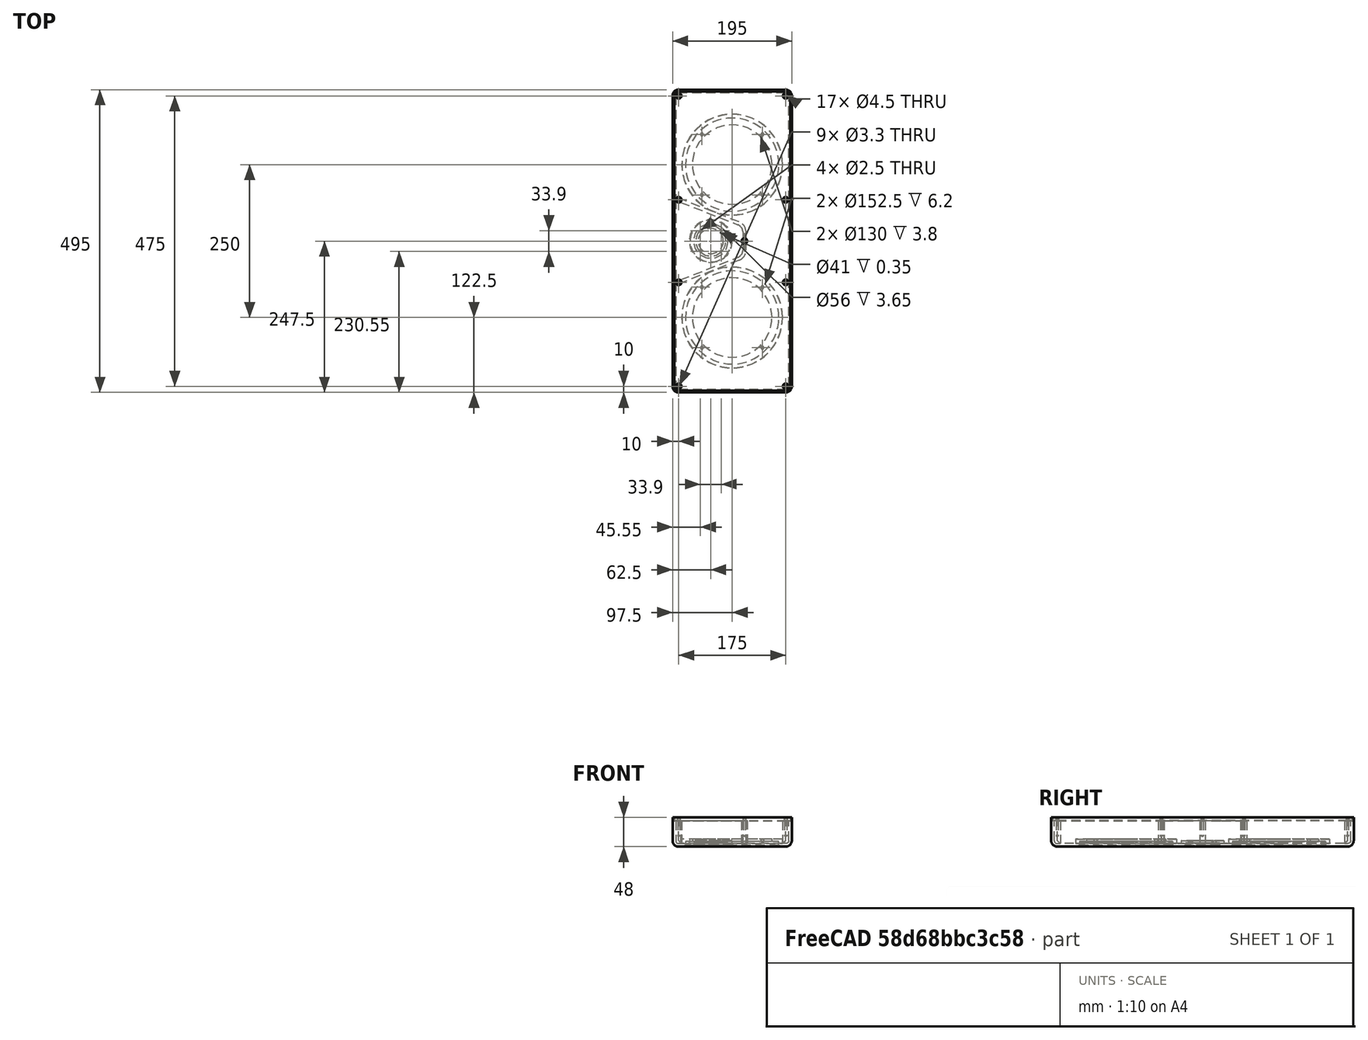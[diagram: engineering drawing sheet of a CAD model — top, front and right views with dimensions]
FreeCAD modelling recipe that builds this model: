
FCSTD DOCUMENT  (FreeCAD 1.1R20260223 (Git shallow))
Label: wallspeakers prototype v6.1
License: All rights reserved
LicenseURL: http://en.wikipedia.org/wiki/All_rights_reserved
objects: TechDraw::DrawViewDimension×43, Sketcher::SketchObject×17, TechDraw::DrawViewAnnotation×7, PartDesign::Pad×6, PartDesign::Pocket×5, TechDraw::DrawProjGroupItem×5, TechDraw::DrawSVGTemplate×4, PartDesign::Hole×4, TechDraw::DrawPage×4, PartDesign::Chamfer×3, App::Point×2, PartDesign::Body×2, TechDraw::DrawViewImage×2, Part::Feature×2, App::VarSet×1, PartDesign::Fillet×1, PartDesign::Thickness×1, App::DocumentObjectGroup×1
note: 167 computed .brp shape members not serialized (recipe doc carries the construction recipe); baked Part::Feature solids carry a one-line shape summary decoded from their .brp

FEATURE [Sketcher::SketchObject] Sketch002  label="base geometry"
  ArcFitTolerance = 1e-06
  AttachmentSupport = -> [XY_Plane]
  ExternalTypes = [0]
  FullyConstrained = true
  MakeInternals = false
  MapMode = 5
  expr: Constraints[3] = <<v>>.bmr_offset
  expr: Constraints[4] = <<v>>.woofer_offset
  expr: Constraints[5] = <<v>>.woofer_offset
  expr: Constraints[6] = <<v>>.ext_height / 2
  expr: Constraints[7] = <<v>>.ext_width / 2
  sketch-geometry (7):
    g0: GeomPoint [constr] X=-97.5 Y=247.5 Z=0
    g1: GeomPoint [constr] X=97.5 Y=247.5 Z=0
    g2: GeomPoint [constr] X=97.5 Y=-247.5 Z=0
    g3: GeomPoint [constr] X=-97.5 Y=-247.5 Z=0
    g4: GeomPoint [constr] X=-35 Y=0 Z=0
    g5: GeomPoint [constr] X=0 Y=125 Z=0
    g6: GeomPoint [constr] X=0 Y=-125 Z=0
  constraints (11):
    c: PointOnObject(g4,g-1)
    c: PointOnObject(g5,g-2)
    c: PointOnObject(g6,g-2)
    c: DistanceX(g4,g-1) = 35
    c: DistanceY(g-1,g5) = 125
    c: DistanceY(g6,g-1) = 125
    c: DistanceY(g-1,g1) = 247.5
    c: DistanceX(g-1,g1) = 97.5
    c: Symmetric(g0,g1,g-2)
    c: Symmetric(g1,g2,g-1)
    c: Symmetric(g3,g2,g-2)
FEATURE [Sketcher::SketchObject] Sketch  label="back panel screw hole geometry"
  ArcFitTolerance = 1e-06
  AttachmentSupport = -> [Sketch002]
  ExternalTypes = [0]
  FullyConstrained = true
  MakeInternals = false
  MapMode = 2
  expr: Constraints[11] = <<v>>.bmr_enc_offset
  expr: Constraints[1] = <<v>>.ext_height / 2 - <<v>>.screw_inset
  expr: Constraints[2] = <<v>>.ext_width / 2 - <<v>>.screw_inset
  expr: Constraints[8] = <<v>>.ext_width / 2 - <<v>>.screw_inset
  expr: Constraints[9] = <<v>>.bmr_enc_base
  sketch-geometry (9):
    g0: GeomPoint [constr] X=-87.5 Y=237.5 Z=0
    g1: GeomPoint [constr] X=87.5 Y=237.5 Z=0
    g2: GeomPoint [constr] X=87.5 Y=-237.5 Z=0
    g3: GeomPoint [constr] X=-87.5 Y=-237.5 Z=0
    g4: GeomPoint [constr] X=-87.5 Y=-67.5 Z=0
    g5: GeomPoint [constr] X=-87.5 Y=67.5 Z=0
    g6: GeomPoint [constr] X=87.5 Y=67.5 Z=0
    g7: GeomPoint [constr] X=87.5 Y=-67.5 Z=0
    g8: GeomPoint [constr] X=20 Y=0 Z=0
  constraints (12):
    c: PointOnObject(g8,g-1)
    c: DistanceY(g-1,g0) = 237.5
    c: DistanceX(g0,g-1) = 87.5
    c: Symmetric(g0,g1,g-2)
    c: Symmetric(g5,g6,g-2)
    c: Symmetric(g4,g7,g-2)
    c: Symmetric(g3,g2,g-2)
    c: Symmetric(g2,g1,g-1)
    c: DistanceX(g5,g-1) = 87.5
    c: DistanceY(g4,g5) = 135
    c: Symmetric(g5,g4,g-1)
    c: DistanceX(g-1,g8) = 20
FEATURE [App::VarSet] VarSet001  label="v"
  backplate_height = 489.8
  backplate_rebate = 5.9
  backplate_thickness = 5
  backplate_width = 189.8
  bmr_enc_base = 135
  bmr_enc_offset = 20
  bmr_enc_top = 50
  bmr_hole_dia = 41
  bmr_offset = 35
  bmr_plate_thickness = 2.75
  bmr_rebate_depth = 5.65
  bmr_rebate_dia = 56
  bmr_support_dia = 70
  bmr_support_thickness = 5
  ext_depth = 48
  ext_height = 495
  ext_roundover = 10
  ext_wall = 5
  ext_width = 195
  gasket_thickness = 0.9
  int_depth = 37.1
  rim_width = 2.5
  screw_inset = 10
  screw_post_diameter = 10
  surround_chamfer = 2
  woofer_cutout_dia = 130
  woofer_offset = 125
  woofer_plate_thickness = 5.3
  woofer_rebate_depth = 8.2
  woofer_rebate_dia = 152.5
  woofer_support_dia = 165
  woofer_support_thickness = 7
  expr: backplate_height = ext_height - rim_width * 2 - 0.2 mm
  expr: backplate_rebate = ext_wall + gasket_thickness
  expr: backplate_width = ext_width - rim_width * 2 - 0.2 mm
  expr: bmr_rebate_depth = bmr_plate_thickness + gasket_thickness + surround_chamfer
  expr: int_depth = ext_depth - ext_wall - backplate_rebate
  expr: woofer_rebate_depth = woofer_plate_thickness + gasket_thickness + surround_chamfer
FEATURE [App::Point] Origin001
  Role = Origin
FEATURE [Sketcher::SketchObject] Sketch003  label="main body"
  ArcFitTolerance = 1e-06
  AttachmentSupport = -> [Sketch002]
  ExternalTypes = [0]
  FullyConstrained = true
  MakeInternals = false
  MapMode = 2
  expr: Constraints[32] = <<v>>.ext_roundover
  expr: Constraints[3] = Sketch002.Constraints[3]
  expr: Constraints[4] = Sketch002.Constraints[4]
  expr: Constraints[5] = Sketch002.Constraints[5]
  expr: Constraints[6] = Sketch002.Constraints[6]
  expr: Constraints[7] = Sketch002.Constraints[7]
  sketch-geometry (17):
    g0: GeomPoint [constr] X=-97.5 Y=247.5 Z=0
    g1: GeomPoint [constr] X=97.5 Y=247.5 Z=0
    g2: GeomPoint [constr] X=97.5 Y=-247.5 Z=0
    g3: GeomPoint [constr] X=-97.5 Y=-247.5 Z=0
    g4: GeomPoint [constr] X=-35 Y=0 Z=0
    g5: GeomPoint [constr] X=0 Y=125 Z=0
    g6: GeomPoint [constr] X=0 Y=-125 Z=0
    g7: LineSegment StartX=-97.5 StartY=237.5 StartZ=0 EndX=-97.5 EndY=-237.5 EndZ=0
    g8: LineSegment StartX=-87.5 StartY=-247.5 StartZ=0 EndX=87.5 EndY=-247.5 EndZ=0
    g9: LineSegment StartX=97.5 StartY=-237.5 StartZ=0 EndX=97.5 EndY=237.5 EndZ=0
    g10: LineSegment StartX=87.5 StartY=247.5 StartZ=0 EndX=-87.5 EndY=247.5 EndZ=0
    g11: ArcOfCircle CenterX=-87.5 CenterY=237.5 CenterZ=0 NormalX=0 NormalY=0 NormalZ=1 AngleXU=0 Radius=10 StartAngle=1.5708 EndAngle=3.14159
    g12: ArcOfCircle CenterX=-87.5 CenterY=-237.5 CenterZ=0 NormalX=0 NormalY=0 NormalZ=1 AngleXU=0 Radius=10 StartAngle=3.14159 EndAngle=4.71239
    g13: ArcOfCircle CenterX=87.5 CenterY=-237.5 CenterZ=0 NormalX=0 NormalY=0 NormalZ=1 AngleXU=0 Radius=10 StartAngle=4.71239 EndAngle=6.28319
    g14: ArcOfCircle CenterX=87.5 CenterY=237.5 CenterZ=0 NormalX=0 NormalY=0 NormalZ=1 AngleXU=0 Radius=10 StartAngle=-3.2e-14 EndAngle=1.5708
    g15: GeomPoint [constr] X=-97.5 Y=247.5 Z=0
    g16: GeomPoint [constr] X=97.5 Y=-247.5 Z=0
  constraints (33):
    c: PointOnObject(g4,g-1)
    c: PointOnObject(g5,g-2)
    c: PointOnObject(g6,g-2)
    c: DistanceX(g4,g-1) = 35
    c: DistanceY(g-1,g5) = 125
    c: DistanceY(g6,g-1) = 125
    c: DistanceY(g-1,g1) = 247.5
    c: DistanceX(g-1,g1) = 97.5
    c: Symmetric(g0,g1,g-2)
    c: Symmetric(g1,g2,g-1)
    c: Symmetric(g3,g2,g-2)
    c: Tangent(g7,g11) = -1.5708
    c: Tangent(g7,g12) = -1.5708
    c: Tangent(g8,g12) = -1.5708
    c: Tangent(g8,g13) = -1.5708
    c: Tangent(g9,g13) = -1.5708
    c: Tangent(g9,g14) = -1.5708
    c: Tangent(g10,g14) = -1.5708
    c: Tangent(g10,g11) = -1.5708
    c: Vertical(g7)
    c: Vertical(g9)
    c: Horizontal(g8)
    c: Horizontal(g10)
    c: Equal(g11,g12)
    c: Equal(g12,g13)
    c: Equal(g13,g14)
    c: PointOnObject(g15,g7)
    c: PointOnObject(g15,g10)
    c: PointOnObject(g16,g8)
    c: PointOnObject(g16,g9)
    c: Coincident(g15,g0)
    c: Coincident(g16,g2)
    c: Radius(g11) = 10
FEATURE [PartDesign::Pad] Pad  label="main body pad"
  Direction = (0,0,1)
  Length = 48
  Length2 = 10
  Profile = -> Sketch003
  ReferenceAxis = -> Sketch003 [N_Axis]
  SideType = 0
  Suppressed = false
  Type = 0
  Type2 = 0
  expr: Length = <<v>>.ext_depth
FEATURE [PartDesign::Fillet] Fillet  label="main body front roundovers"
  Base = -> Pad [Face9]
  BaseFeature = -> Pad
  Radius = 10
  SupportTransform = false
  Suppressed = false
  UseAllEdges = false
  expr: Radius = <<v>>.ext_roundover
FEATURE [PartDesign::Thickness] Thickness  label="main body thicknessing"
  Base = -> Fillet [Face4]
  BaseFeature = -> Fillet
  Intersection = false
  Join = 0
  Mode = 0
  Reversed = true
  SupportTransform = false
  Suppressed = false
  Value = 5
  expr: Value = <<v>>.ext_wall
FEATURE [Sketcher::SketchObject] Sketch004  label="screw posts layout"
  ArcFitTolerance = 1e-06
  AttachmentOffset = pos=(0,0,5) rot=(0,0,1;0rad)
  AttachmentSupport = -> [Sketch]
  ExternalTypes = [0]
  FullyConstrained = true
  MakeInternals = false
  MapMode = 2
  Placement = pos=(0,0,5) rot=(0,0,1;0rad)
  expr: .AttachmentOffset.Base.z = <<v>>.ext_wall
  expr: Constraints[12] = <<v>>.bmr_enc_offset
  expr: Constraints[13] = <<v>>.screw_post_diameter
  expr: Constraints[1] = Sketch.Constraints[1]
  expr: Constraints[22] = <<v>>.screw_post_diameter
  expr: Constraints[2] = Sketch.Constraints[2]
  expr: Constraints[8] = Sketch.Constraints[8]
  expr: Constraints[9] = Sketch.Constraints[9]
  sketch-geometry (18):
    g0: GeomPoint [constr] X=-87.5 Y=237.5 Z=0
    g1: GeomPoint [constr] X=87.5 Y=237.5 Z=0
    g2: GeomPoint [constr] X=87.5 Y=-237.5 Z=0
    g3: GeomPoint [constr] X=-87.5 Y=-237.5 Z=0
    g4: GeomPoint [constr] X=-87.5 Y=-67.5 Z=0
    g5: GeomPoint [constr] X=-87.5 Y=67.5 Z=0
    g6: GeomPoint [constr] X=87.5 Y=67.5 Z=0
    g7: GeomPoint [constr] X=87.5 Y=-67.5 Z=0
    g8: GeomPoint [constr] X=20 Y=0 Z=0
    g9: Circle CenterX=20 CenterY=0 CenterZ=0 NormalX=0 NormalY=0 NormalZ=1 AngleXU=0 Radius=5
    g10: Circle CenterX=-87.5 CenterY=237.5 CenterZ=0 NormalX=0 NormalY=0 NormalZ=1 AngleXU=0 Radius=5
    g11: Circle CenterX=87.5 CenterY=237.5 CenterZ=0 NormalX=0 NormalY=0 NormalZ=1 AngleXU=0 Radius=5
    g12: Circle CenterX=87.5 CenterY=67.5 CenterZ=0 NormalX=0 NormalY=0 NormalZ=1 AngleXU=0 Radius=5
    g13: Circle CenterX=-87.5 CenterY=67.5 CenterZ=0 NormalX=0 NormalY=0 NormalZ=1 AngleXU=0 Radius=5
    g14: Circle CenterX=87.5 CenterY=-67.5 CenterZ=0 NormalX=0 NormalY=0 NormalZ=1 AngleXU=0 Radius=5
    g15: Circle CenterX=-87.5 CenterY=-67.5 CenterZ=0 NormalX=0 NormalY=0 NormalZ=1 AngleXU=0 Radius=5
    g16: Circle CenterX=-87.5 CenterY=-237.5 CenterZ=0 NormalX=0 NormalY=0 NormalZ=1 AngleXU=0 Radius=5
    g17: Circle CenterX=87.5 CenterY=-237.5 CenterZ=0 NormalX=0 NormalY=0 NormalZ=1 AngleXU=0 Radius=5
  constraints (30):
    c: PointOnObject(g8,g-1)
    c: DistanceY(g-1,g0) = 237.5
    c: DistanceX(g0,g-1) = 87.5
    c: Symmetric(g0,g1,g-2)
    c: Symmetric(g5,g6,g-2)
    c: Symmetric(g4,g7,g-2)
    c: Symmetric(g3,g2,g-2)
    c: Symmetric(g2,g1,g-1)
    c: DistanceX(g5,g-1) = 87.5
    c: DistanceY(g4,g5) = 135
    c: Symmetric(g5,g4,g-1)
    c: Coincident(g9,g8)
    c: DistanceX(g-1,g8) = 20
    c: Diameter(g9) = 10
    c: Coincident(g10,g0)
    c: Coincident(g11,g1)
    c: Coincident(g12,g6)
    c: Coincident(g13,g5)
    c: Coincident(g14,g7)
    c: Coincident(g15,g4)
    c: Coincident(g16,g3)
    c: Coincident(g17,g2)
    c: Diameter(g10) = 10
    c: Equal(g10,g11)
    c: Equal(g11,g12)
    c: Equal(g12,g13)
    c: Equal(g13,g15)
    c: Equal(g15,g14)
    c: Equal(g14,g17)
    c: Equal(g17,g16)
FEATURE [Sketcher::SketchObject] Sketch005  label="woofer rebates"
  ArcFitTolerance = 1e-06
  AttachmentSupport = -> [Origin]
  ExternalTypes = [0]
  FullyConstrained = true
  MakeInternals = false
  MapMode = 5
  expr: Constraints[12] = VarSet001.woofer_rebate_dia
  expr: Constraints[3] = Sketch002.Constraints[3]
  expr: Constraints[4] = Sketch002.Constraints[4]
  expr: Constraints[5] = Sketch002.Constraints[5]
  expr: Constraints[6] = Sketch002.Constraints[6]
  expr: Constraints[7] = Sketch002.Constraints[7]
  sketch-geometry (9):
    g0: GeomPoint [constr] X=-97.5 Y=247.5 Z=0
    g1: GeomPoint [constr] X=97.5 Y=247.5 Z=0
    g2: GeomPoint [constr] X=97.5 Y=-247.5 Z=0
    g3: GeomPoint [constr] X=-97.5 Y=-247.5 Z=0
    g4: GeomPoint [constr] X=-35 Y=0 Z=0
    g5: GeomPoint [constr] X=0 Y=125 Z=0
    g6: GeomPoint [constr] X=0 Y=-125 Z=0
    g7: Circle CenterX=0 CenterY=125 CenterZ=0 NormalX=0 NormalY=0 NormalZ=1 AngleXU=0 Radius=76.25
    g8: Circle CenterX=0 CenterY=-125 CenterZ=0 NormalX=0 NormalY=0 NormalZ=1 AngleXU=0 Radius=76.25
  constraints (15):
    c: PointOnObject(g4,g-1)
    c: PointOnObject(g5,g-2)
    c: PointOnObject(g6,g-2)
    c: DistanceX(g4,g-1) = 35
    c: DistanceY(g-1,g5) = 125
    c: DistanceY(g6,g-1) = 125
    c: DistanceY(g-1,g1) = 247.5
    c: DistanceX(g-1,g1) = 97.5
    c: Symmetric(g0,g1,g-2)
    c: Symmetric(g1,g2,g-1)
    c: Symmetric(g3,g2,g-2)
    c: Coincident(g8,g6)
    c: Diameter(g7) = 152.5
    c: Equal(g7,g8)
    c: Coincident(g5,g7)
FEATURE [Sketcher::SketchObject] Sketch006
  ArcFitTolerance = 1e-06
  AttachmentOffset = pos=(0,0,5) rot=(0,0,1;0rad)
  AttachmentSupport = -> [Origin]
  ExternalTypes = [0]
  FullyConstrained = true
  MakeInternals = false
  MapMode = 5
  Placement = pos=(0,0,5) rot=(0,0,1;0rad)
  expr: .AttachmentOffset.Base.z = <<v>>.ext_wall
  expr: Constraints[14] = Sketch002.Constraints[3]
  expr: Constraints[15] = Sketch002.Constraints[4]
  expr: Constraints[16] = Sketch002.Constraints[5]
  expr: Constraints[17] = Sketch002.Constraints[6]
  expr: Constraints[18] = Sketch002.Constraints[7]
  expr: Constraints[22] = VarSet001.woofer_support_dia
  expr: Constraints[3] = Sketch002.Constraints[3]
  expr: Constraints[4] = Sketch002.Constraints[4]
  expr: Constraints[5] = Sketch002.Constraints[5]
  expr: Constraints[6] = Sketch002.Constraints[6]
  expr: Constraints[7] = Sketch002.Constraints[7]
  sketch-geometry (16):
    g0: GeomPoint [constr] X=-97.5 Y=247.5 Z=0
    g1: GeomPoint [constr] X=97.5 Y=247.5 Z=0
    g2: GeomPoint [constr] X=97.5 Y=-247.5 Z=0
    g3: GeomPoint [constr] X=-97.5 Y=-247.5 Z=0
    g4: GeomPoint [constr] X=-35 Y=0 Z=0
    g5: GeomPoint [constr] X=0 Y=125 Z=0
    g6: GeomPoint [constr] X=0 Y=-125 Z=0
    g7: GeomPoint [constr] X=-97.5 Y=247.5 Z=0
    g8: GeomPoint [constr] X=97.5 Y=247.5 Z=0
    g9: GeomPoint [constr] X=97.5 Y=-247.5 Z=0
    g10: GeomPoint [constr] X=-97.5 Y=-247.5 Z=0
    g11: GeomPoint [constr] X=-35 Y=0 Z=0
    g12: GeomPoint [constr] X=0 Y=125 Z=0
    g13: GeomPoint [constr] X=0 Y=-125 Z=0
    g14: Circle CenterX=0 CenterY=125 CenterZ=0 NormalX=0 NormalY=0 NormalZ=1 AngleXU=0 Radius=82.5
    g15: Circle CenterX=0 CenterY=-125 CenterZ=0 NormalX=0 NormalY=0 NormalZ=1 AngleXU=0 Radius=82.5
  constraints (26):
    c: PointOnObject(g4,g-1)
    c: PointOnObject(g5,g-2)
    c: PointOnObject(g6,g-2)
    c: DistanceX(g4,g-1) = 35
    c: DistanceY(g-1,g5) = 125
    c: DistanceY(g6,g-1) = 125
    c: DistanceY(g-1,g1) = 247.5
    c: DistanceX(g-1,g1) = 97.5
    c: Symmetric(g0,g1,g-2)
    c: Symmetric(g1,g2,g-1)
    c: Symmetric(g3,g2,g-2)
    c: PointOnObject(g11,g-1)
    c: PointOnObject(g12,g-2)
    c: PointOnObject(g13,g-2)
    c: DistanceX(g11,g-1) = 35
    c: DistanceY(g-1,g12) = 125
    c: DistanceY(g13,g-1) = 125
    c: DistanceY(g-1,g8) = 247.5
    c: DistanceX(g-1,g8) = 97.5
    c: Symmetric(g7,g8,g-2)
    c: Symmetric(g8,g9,g-1)
    c: Symmetric(g10,g9,g-2)
    c: Diameter(g14) = 165
    c: Coincident(g15,g6)
    c: Equal(g14,g15)
    c: Coincident(g14,g5)
FEATURE [Sketcher::SketchObject] Sketch007
  ArcFitTolerance = 1e-06
  AttachmentSupport = -> [Origin]
  ExternalTypes = [0]
  FullyConstrained = true
  MakeInternals = false
  MapMode = 5
  expr: Constraints[12] = VarSet001.woofer_cutout_dia
  expr: Constraints[3] = Sketch002.Constraints[3]
  expr: Constraints[4] = Sketch002.Constraints[4]
  expr: Constraints[5] = Sketch002.Constraints[5]
  expr: Constraints[6] = Sketch002.Constraints[6]
  expr: Constraints[7] = Sketch002.Constraints[7]
  sketch-geometry (9):
    g0: GeomPoint [constr] X=-97.5 Y=247.5 Z=0
    g1: GeomPoint [constr] X=97.5 Y=247.5 Z=0
    g2: GeomPoint [constr] X=97.5 Y=-247.5 Z=0
    g3: GeomPoint [constr] X=-97.5 Y=-247.5 Z=0
    g4: GeomPoint [constr] X=-35 Y=0 Z=0
    g5: GeomPoint [constr] X=0 Y=125 Z=0
    g6: GeomPoint [constr] X=0 Y=-125 Z=0
    g7: Circle CenterX=0 CenterY=125 CenterZ=0 NormalX=0 NormalY=0 NormalZ=1 AngleXU=0 Radius=65
    g8: Circle CenterX=0 CenterY=-125 CenterZ=0 NormalX=0 NormalY=0 NormalZ=1 AngleXU=0 Radius=65
  constraints (15):
    c: PointOnObject(g4,g-1)
    c: PointOnObject(g5,g-2)
    c: PointOnObject(g6,g-2)
    c: DistanceX(g4,g-1) = 35
    c: DistanceY(g-1,g5) = 125
    c: DistanceY(g6,g-1) = 125
    c: DistanceY(g-1,g1) = 247.5
    c: DistanceX(g-1,g1) = 97.5
    c: Symmetric(g0,g1,g-2)
    c: Symmetric(g1,g2,g-1)
    c: Symmetric(g3,g2,g-2)
    c: Coincident(g7,g5)
    c: Diameter(g7) = 130
    c: Equal(g7,g8)
    c: Coincident(g8,g6)
FEATURE [Sketcher::SketchObject] Sketch008  label="bmr rebate"
  ArcFitTolerance = 1e-06
  AttachmentSupport = -> [Origin]
  ExternalTypes = [0]
  FullyConstrained = true
  MakeInternals = false
  MapMode = 5
  expr: Constraints[11] = VarSet001.bmr_rebate_dia
  expr: Constraints[3] = <<v>>.bmr_offset
  expr: Constraints[4] = Sketch002.Constraints[4]
  expr: Constraints[5] = Sketch002.Constraints[5]
  expr: Constraints[6] = Sketch002.Constraints[6]
  expr: Constraints[7] = Sketch002.Constraints[7]
  sketch-geometry (8):
    g0: GeomPoint [constr] X=-97.5 Y=247.5 Z=0
    g1: GeomPoint [constr] X=97.5 Y=247.5 Z=0
    g2: GeomPoint [constr] X=97.5 Y=-247.5 Z=0
    g3: GeomPoint [constr] X=-97.5 Y=-247.5 Z=0
    g4: GeomPoint [constr] X=-35 Y=0 Z=0
    g5: GeomPoint [constr] X=0 Y=125 Z=0
    g6: GeomPoint [constr] X=0 Y=-125 Z=0
    g7: Circle CenterX=-35 CenterY=0 CenterZ=0 NormalX=0 NormalY=0 NormalZ=1 AngleXU=0 Radius=28
  constraints (13):
    c: PointOnObject(g4,g-1)
    c: PointOnObject(g5,g-2)
    c: PointOnObject(g6,g-2)
    c: DistanceX(g4,g-1) = 35
    c: DistanceY(g-1,g5) = 125
    c: DistanceY(g6,g-1) = 125
    c: DistanceY(g-1,g1) = 247.5
    c: DistanceX(g-1,g1) = 97.5
    c: Symmetric(g0,g1,g-2)
    c: Symmetric(g1,g2,g-1)
    c: Symmetric(g3,g2,g-2)
    c: Diameter(g7) = 56
    c: Coincident(g7,g4)
FEATURE [Sketcher::SketchObject] Sketch009  label="bmr_support"
  ArcFitTolerance = 1e-06
  AttachmentOffset = pos=(0,0,5) rot=(0,0,1;0rad)
  AttachmentSupport = -> [Sketch008]
  ExternalTypes = [0]
  FullyConstrained = true
  MakeInternals = false
  MapMode = 2
  Placement = pos=(0,0,5) rot=(0,0,1;0rad)
  expr: .AttachmentOffset.Base.z = <<v>>.ext_wall
  expr: Constraints[12] = VarSet001.bmr_support_dia
  expr: Constraints[3] = Sketch002.Constraints[3]
  expr: Constraints[4] = Sketch002.Constraints[4]
  expr: Constraints[5] = Sketch002.Constraints[5]
  expr: Constraints[6] = Sketch002.Constraints[6]
  expr: Constraints[7] = Sketch002.Constraints[7]
  sketch-geometry (8):
    g0: GeomPoint [constr] X=-97.5 Y=247.5 Z=0
    g1: GeomPoint [constr] X=97.5 Y=247.5 Z=0
    g2: GeomPoint [constr] X=97.5 Y=-247.5 Z=0
    g3: GeomPoint [constr] X=-97.5 Y=-247.5 Z=0
    g4: GeomPoint [constr] X=-35 Y=0 Z=0
    g5: GeomPoint [constr] X=0 Y=125 Z=0
    g6: GeomPoint [constr] X=0 Y=-125 Z=0
    g7: Circle CenterX=-35 CenterY=0 CenterZ=0 NormalX=0 NormalY=0 NormalZ=1 AngleXU=0 Radius=35
  constraints (13):
    c: PointOnObject(g4,g-1)
    c: PointOnObject(g5,g-2)
    c: PointOnObject(g6,g-2)
    c: DistanceX(g4,g-1) = 35
    c: DistanceY(g-1,g5) = 125
    c: DistanceY(g6,g-1) = 125
    c: DistanceY(g-1,g1) = 247.5
    c: DistanceX(g-1,g1) = 97.5
    c: Symmetric(g0,g1,g-2)
    c: Symmetric(g1,g2,g-1)
    c: Symmetric(g3,g2,g-2)
    c: Coincident(g7,g4)
    c: Diameter(g7) = 70
FEATURE [Sketcher::SketchObject] Sketch010
  ArcFitTolerance = 1e-06
  AttachmentSupport = -> [Origin]
  ExternalTypes = [0]
  FullyConstrained = true
  MakeInternals = false
  MapMode = 5
  expr: Constraints[12] = <<v>>.bmr_hole_dia
  expr: Constraints[3] = <<v>>.bmr_offset
  expr: Constraints[4] = Sketch002.Constraints[4]
  expr: Constraints[5] = Sketch002.Constraints[5]
  expr: Constraints[6] = Sketch002.Constraints[6]
  expr: Constraints[7] = Sketch002.Constraints[7]
  sketch-geometry (8):
    g0: GeomPoint [constr] X=-97.5 Y=247.5 Z=0
    g1: GeomPoint [constr] X=97.5 Y=247.5 Z=0
    g2: GeomPoint [constr] X=97.5 Y=-247.5 Z=0
    g3: GeomPoint [constr] X=-97.5 Y=-247.5 Z=0
    g4: GeomPoint [constr] X=-35 Y=0 Z=0
    g5: GeomPoint [constr] X=0 Y=125 Z=0
    g6: GeomPoint [constr] X=0 Y=-125 Z=0
    g7: Circle CenterX=-35 CenterY=0 CenterZ=0 NormalX=0 NormalY=0 NormalZ=1 AngleXU=0 Radius=20.5
  constraints (13):
    c: PointOnObject(g4,g-1)
    c: PointOnObject(g5,g-2)
    c: PointOnObject(g6,g-2)
    c: DistanceX(g4,g-1) = 35
    c: DistanceY(g-1,g5) = 125
    c: DistanceY(g6,g-1) = 125
    c: DistanceY(g-1,g1) = 247.5
    c: DistanceX(g-1,g1) = 97.5
    c: Symmetric(g0,g1,g-2)
    c: Symmetric(g1,g2,g-1)
    c: Symmetric(g3,g2,g-2)
    c: Coincident(g7,g4)
    c: Diameter(g7) = 41
FEATURE [Sketcher::SketchObject] Sketch011  label="woofer screw hole layout"
  ArcFitTolerance = 1e-06
  AttachmentOffset = pos=(0,0,8.2) rot=(0,0,1;0rad)
  AttachmentSupport = -> [Origin]
  ExternalTypes = [0]
  FullyConstrained = true
  MakeInternals = false
  MapMode = 5
  Placement = pos=(0,0,8.2) rot=(0,0,1;0rad)
  expr: .AttachmentOffset.Base.z = <<v>>.woofer_rebate_depth
  expr: Constraints[4] = <<v>>.woofer_offset
  expr: Constraints[5] = <<v>>.woofer_offset
  sketch-geometry (10):
    g0: GeomPoint X=-49.53 Y=174.53 Z=0
    g1: GeomPoint X=49.53 Y=174.53 Z=0
    g2: GeomPoint X=49.53 Y=75.47 Z=0
    g3: GeomPoint X=-49.53 Y=75.47 Z=0
    g4: GeomPoint X=49.53 Y=-75.47 Z=0
    g5: GeomPoint X=-49.53 Y=-75.47 Z=0
    g6: GeomPoint X=-49.53 Y=-174.53 Z=0
    g7: GeomPoint X=49.53 Y=-174.53 Z=0
    g8: LineSegment [constr] StartX=100 StartY=-125 StartZ=0 EndX=-100 EndY=-125 EndZ=0
    g9: LineSegment [constr] StartX=100 StartY=125 StartZ=0 EndX=-100 EndY=125 EndZ=0
  constraints (16):
    c: DistanceX(g9,g9) = 200
    c: DistanceX(g8,g8) = 200
    c: Symmetric(g9,g9,g-2)
    c: Symmetric(g8,g8,g-2)
    c: Distance(g-1,g9) = 125
    c: Distance(g-1,g8) = 125
    c: Distance(g1,g9) = 49.53
    c: DistanceX(g-1,g1) = 49.53
    c: Symmetric(g1,g0,g-2)
    c: Symmetric(g0,g3,g9)
    c: Symmetric(g1,g2,g9)
    c: Distance(g4,g8) = 49.53
    c: Distance(g4,g-2) = 49.53
    c: Symmetric(g4,g5,g-2)
    c: Symmetric(g5,g6,g8)
    c: Symmetric(g4,g7,g8)
FEATURE [Sketcher::SketchObject] Sketch012  label="bmr screw hole layout"
  ArcFitTolerance = 1e-06
  AttachmentOffset = pos=(0,0,5.65) rot=(0,0,1;0rad)
  AttachmentSupport = -> [Origin]
  ExternalTypes = [0]
  FullyConstrained = true
  MakeInternals = false
  MapMode = 5
  Placement = pos=(0,0,5.65) rot=(0,0,1;0rad)
  expr: .AttachmentOffset.Base.z = <<v>>.bmr_rebate_depth
  expr: Constraints[0] = <<v>>.bmr_offset
  sketch-geometry (5):
    g0: LineSegment [constr] StartX=-35 StartY=50 StartZ=0 EndX=-35 EndY=-50 EndZ=0
    g1: GeomPoint X=-51.95 Y=16.95 Z=0
    g2: GeomPoint X=-18.05 Y=16.95 Z=0
    g3: GeomPoint X=-18.05 Y=-16.95 Z=0
    g4: GeomPoint X=-51.95 Y=-16.95 Z=0
  constraints (8):
    c: Distance(g-2,g0) = 35
    c: DistanceY(g0,g0) = 100
    c: Symmetric(g0,g0,g-1)
    c: Distance(g1,g-1) = 16.95
    c: Distance(g1,g0) = 16.95
    c: Symmetric(g1,g2,g0)
    c: Symmetric(g1,g4,g-1)
    c: Symmetric(g2,g3,g-1)
FEATURE [Sketcher::SketchObject] Sketch013  label="post screw hole layout"
  ArcFitTolerance = 1e-06
  AttachmentOffset = pos=(0,0,42.1) rot=(0,0,1;0rad)
  AttachmentSupport = -> [Origin]
  ExternalTypes = [0]
  FullyConstrained = true
  MakeInternals = false
  MapMode = 5
  Placement = pos=(0,0,42.1) rot=(0,0,1;0rad)
  expr: .AttachmentOffset.Base.z = <<v>>.int_depth + <<v>>.ext_wall
  expr: Constraints[11] = Sketch.Constraints[11]
  expr: Constraints[1] = Sketch.Constraints[1]
  expr: Constraints[2] = Sketch.Constraints[2]
  expr: Constraints[8] = Sketch.Constraints[8]
  expr: Constraints[9] = Sketch.Constraints[9]
  sketch-geometry (9):
    g0: GeomPoint X=-87.5 Y=237.5 Z=0
    g1: GeomPoint X=87.5 Y=237.5 Z=0
    g2: GeomPoint X=87.5 Y=-237.5 Z=0
    g3: GeomPoint X=-87.5 Y=-237.5 Z=0
    g4: GeomPoint X=-87.5 Y=-67.5 Z=0
    g5: GeomPoint X=-87.5 Y=67.5 Z=0
    g6: GeomPoint X=87.5 Y=67.5 Z=0
    g7: GeomPoint X=87.5 Y=-67.5 Z=0
    g8: GeomPoint X=20 Y=0 Z=0
  constraints (12):
    c: PointOnObject(g8,g-1)
    c: DistanceY(g-1,g0) = 237.5
    c: DistanceX(g0,g-1) = 87.5
    c: Symmetric(g0,g1,g-2)
    c: Symmetric(g5,g6,g-2)
    c: Symmetric(g4,g7,g-2)
    c: Symmetric(g3,g2,g-2)
    c: Symmetric(g2,g1,g-1)
    c: DistanceX(g5,g-1) = 87.5
    c: DistanceY(g4,g5) = 135
    c: Symmetric(g5,g4,g-1)
    c: DistanceX(g-1,g8) = 20
FEATURE [Sketcher::SketchObject] Sketch014  label="rim pocket outline"
  ArcFitTolerance = 1e-06
  AttachmentOffset = pos=(0,0,48) rot=(0,0,1;0rad)
  AttachmentSupport = -> [Origin]
  ExternalTypes = [0]
  FullyConstrained = true
  MakeInternals = false
  MapMode = 5
  Placement = pos=(0,0,48) rot=(0,0,1;0rad)
  expr: .AttachmentOffset.Base.z = <<v>>.ext_depth
  expr: Constraints[17] = <<v>>.ext_roundover - <<v>>.rim_width
  expr: Constraints[18] = <<v>>.ext_width - <<v>>.rim_width * 2
  expr: Constraints[19] = <<v>>.ext_height - <<v>>.rim_width * 2
  sketch-geometry (10):
    g0: LineSegment StartX=-95 StartY=237.5 StartZ=0 EndX=-95 EndY=-237.5 EndZ=0
    g1: LineSegment StartX=-87.5 StartY=-245 StartZ=0 EndX=87.5 EndY=-245 EndZ=0
    g2: LineSegment StartX=95 StartY=-237.5 StartZ=0 EndX=95 EndY=237.5 EndZ=0
    g3: LineSegment StartX=87.5 StartY=245 StartZ=0 EndX=-87.5 EndY=245 EndZ=0
    g4: ArcOfCircle CenterX=-87.5 CenterY=237.5 CenterZ=0 NormalX=0 NormalY=0 NormalZ=1 AngleXU=0 Radius=7.5 StartAngle=1.5708 EndAngle=3.14159
    g5: ArcOfCircle CenterX=-87.5 CenterY=-237.5 CenterZ=0 NormalX=0 NormalY=0 NormalZ=1 AngleXU=0 Radius=7.5 StartAngle=3.14159 EndAngle=4.71239
    g6: ArcOfCircle CenterX=87.5 CenterY=-237.5 CenterZ=0 NormalX=0 NormalY=0 NormalZ=1 AngleXU=0 Radius=7.5 StartAngle=4.71239 EndAngle=6.28319
    g7: ArcOfCircle CenterX=87.5 CenterY=237.5 CenterZ=0 NormalX=0 NormalY=0 NormalZ=1 AngleXU=0 Radius=7.5 StartAngle=1.6e-15 EndAngle=1.5708
    g8: GeomPoint [constr] X=-95 Y=245 Z=0
    g9: GeomPoint [constr] X=95 Y=-245 Z=0
  constraints (22):
    c: Tangent(g0,g4) = -1.5708
    c: Tangent(g0,g5) = -1.5708
    c: Tangent(g1,g5) = -1.5708
    c: Tangent(g1,g6) = -1.5708
    c: Tangent(g2,g6) = -1.5708
    c: Tangent(g2,g7) = -1.5708
    c: Tangent(g3,g7) = -1.5708
    c: Tangent(g3,g4) = -1.5708
    c: Vertical(g0)
    c: Vertical(g2)
    c: Horizontal(g1)
    c: Equal(g5,g6)
    c: Equal(g6,g7)
    c: PointOnObject(g8,g0)
    c: PointOnObject(g8,g3)
    c: PointOnObject(g9,g1)
    c: PointOnObject(g9,g2)
    c: Radius(g4) = 7.5
    c: Distance(g2,g0) = 190
    c: Distance(g1,g3) = 490
    c: Symmetric(g3,g3,g-2)
    c: Symmetric(g3,g1,g-1)
FEATURE [Sketcher::SketchObject] Sketch015  label="interior baffle path"
  ArcFitTolerance = 1e-06
  AttachmentOffset = pos=(0,0,5) rot=(0,0,1;0rad)
  AttachmentSupport = -> [Sketch]
  ExternalTypes = [0]
  FullyConstrained = true
  MakeInternals = false
  MapMode = 2
  Placement = pos=(0,0,5) rot=(0,0,1;0rad)
  expr: .AttachmentOffset.Base.z = <<v>>.ext_wall
  expr: Constraints[1] = Sketch.Constraints[8] - 2 mm
  expr: Constraints[2] = Sketch.Constraints[9] - 2 mm
  expr: Constraints[4] = Sketch.Constraints[11]
  sketch-geometry (20):
    g0: GeomPoint [constr] X=-85.5 Y=-66.5 Z=0
    g1: GeomPoint [constr] X=-85.5 Y=66.5 Z=0
    g2: GeomPoint [constr] X=20 Y=0 Z=0
    g3: LineSegment [constr] StartX=-85.5 StartY=66.5 StartZ=0 EndX=10.4634 EndY=28.9697 EndZ=0
    g4: LineSegment [constr] StartX=20 StartY=-15 StartZ=0 EndX=20 EndY=15 EndZ=0
    g5: LineSegment [constr] StartX=-85.5 StartY=-66.5 StartZ=0 EndX=10.4634 EndY=-28.9697 EndZ=0
    g6: ArcOfCircle [constr] CenterX=5 CenterY=15 CenterZ=0 NormalX=0 NormalY=0 NormalZ=1 AngleXU=0 Radius=15 StartAngle=0 EndAngle=1.19799
    g7: ArcOfCircle [constr] CenterX=5 CenterY=-15 CenterZ=0 NormalX=0 NormalY=0 NormalZ=1 AngleXU=0 Radius=15 StartAngle=5.08519 EndAngle=6.28319
    g8: LineSegment StartX=17.5 StartY=15 StartZ=0 EndX=17.5 EndY=-15 EndZ=0
    g9: LineSegment StartX=22.5 StartY=-15 StartZ=0 EndX=22.5 EndY=15 EndZ=0
    g10: LineSegment StartX=11.374 StartY=31.2979 StartZ=0 EndX=-84.5894 EndY=68.8283 EndZ=0
    g11: LineSegment StartX=-84.5894 StartY=68.8283 StartZ=0 EndX=-86.4106 EndY=64.1717 EndZ=0
    g12: LineSegment StartX=-86.4106 StartY=64.1717 StartZ=0 EndX=9.55283 EndY=26.6414 EndZ=0
    g13: LineSegment StartX=-86.4106 StartY=-64.1717 StartZ=0 EndX=9.55283 EndY=-26.6414 EndZ=0
    g14: LineSegment StartX=11.374 StartY=-31.2979 StartZ=0 EndX=-84.5894 EndY=-68.8283 EndZ=0
    g15: LineSegment StartX=-84.5894 StartY=-68.8283 StartZ=0 EndX=-86.4106 EndY=-64.1717 EndZ=0
    g16: ArcOfCircle CenterX=5 CenterY=-15 CenterZ=0 NormalX=0 NormalY=0 NormalZ=1 AngleXU=0 Radius=12.5 StartAngle=5.08519 EndAngle=6.28319
    g17: ArcOfCircle CenterX=5 CenterY=-15 CenterZ=0 NormalX=0 NormalY=0 NormalZ=1 AngleXU=0 Radius=17.5 StartAngle=5.08519 EndAngle=6.28319
    g18: ArcOfCircle CenterX=5 CenterY=15 CenterZ=0 NormalX=0 NormalY=0 NormalZ=1 AngleXU=0 Radius=12.5 StartAngle=-9e-16 EndAngle=1.19799
    g19: ArcOfCircle CenterX=5 CenterY=15 CenterZ=0 NormalX=0 NormalY=0 NormalZ=1 AngleXU=0 Radius=17.5 StartAngle=0 EndAngle=1.19799
  constraints (45):
    c: PointOnObject(g2,g-1)
    c: DistanceX(g1,g-1) = 85.5
    c: DistanceY(g0,g1) = 133
    c: Symmetric(g1,g0,g-1)
    c: DistanceX(g-1,g2) = 20
    c: Coincident(g5,g0)
    c: Symmetric(g4,g4,g-1)
    c: DistanceY(g4,g4) = 30
    c: Tangent(g7,g5) = -1.5708
    c: Tangent(g6,g3) = 1.5708
    c: Tangent(g6,g4) = -1.5708
    c: Tangent(g7,g4) = -1.5708
    c: Radius(g6) = 15
    c: Radius(g7) = 15
    c: PointOnObject(g2,g4)
    c: Coincident(g3,g1)
    c: Vertical(g9)
    c: Coincident(g15,g14)
    c: Coincident(g15,g13)
    c: Parallel(g12,g10)
    c: Parallel(g13,g14)
    c: Parallel(g10,g3)
    c: Parallel(g13,g5)
    c: Coincident(g10,g11)
    c: Coincident(g12,g11)
    c: Distance(g11,g11) = 5
    c: Symmetric(g10,g11,g3)
    c: Symmetric(g9,g8,g4)
    c: DistanceX(g8,g9) = 5
    c: DistanceY(g9,g9) = 30
    c: Symmetric(g8,g8,g-1)
    c: Distance(g15,g15) = 5
    c: Symmetric(g13,g14,g5)
    c: Equal(g5,g13)
    c: Equal(g5,g14)
    c: Equal(g3,g10)
    c: Equal(g3,g12)
    c: Coincident(g18,g8)
    c: Tangent(g16,g8) = 1.5708
    c: Tangent(g16,g13) = -1.5708
    c: Tangent(g17,g9) = -1.5708
    c: Tangent(g17,g14) = 1.5708
    c: Tangent(g18,g12) = 1.5708
    c: Tangent(g19,g10) = -1.5708
    c: Tangent(g19,g9) = -1.5708
FEATURE [TechDraw::DrawSVGTemplate] Template001
  Height = 210
  Orientation = 1
  Template = /Applications/FreeCAD.app/Contents/Resources/share/Mod/TechDraw/Templates/ISO/A4_Landscape_TD.svg
  Width = 297
FEATURE [TechDraw::DrawSVGTemplate] Template
  Height = 210
  Orientation = 1
  Template = /Applications/FreeCAD.app/Contents/Resources/share/Mod/TechDraw/Templates/ISO/A4_Landscape_TD.svg
  Width = 297
FEATURE [TechDraw::DrawSVGTemplate] Template002
  Height = 210
  Orientation = 1
  Template = /Applications/FreeCAD.app/Contents/Resources/share/Mod/TechDraw/Templates/ISO/A4_Landscape_TD.svg
  Width = 297
FEATURE [PartDesign::Pocket] Pocket004  label="rim pocket"
  BaseFeature = -> Thickness
  Direction = (0,0,-1)
  Length = 5.9
  Length2 = 5
  Profile = -> Sketch014
  ReferenceAxis = -> Sketch014 [N_Axis]
  SideType = 0
  Suppressed = false
  Type = 0
  Type2 = 0
  expr: Length = <<v>>.backplate_rebate
FEATURE [PartDesign::Pad] Pad004  label="interior baffle"
  BaseFeature = -> Pocket004
  Direction = (0,0,1)
  Length = 37.1
  Length2 = 10
  Profile = -> Sketch015
  ReferenceAxis = -> Sketch015 [N_Axis]
  SideType = 0
  Suppressed = false
  Type = 0
  Type2 = 0
  expr: Length = <<v>>.int_depth
FEATURE [PartDesign::Pad] Pad002  label="woofer support ring"
  BaseFeature = -> Pad004
  Direction = (0,0,1)
  Length = 7
  Length2 = 10
  Profile = -> Sketch006
  ReferenceAxis = -> Sketch006 [N_Axis]
  SideType = 0
  Suppressed = false
  Type = 0
  Type2 = 0
  expr: Length = VarSet001.woofer_support_thickness
FEATURE [PartDesign::Pocket] Pocket  label="woofer rebate pocket"
  BaseFeature = -> Pad002
  Direction = (0,0,-1)
  Length = 8.2
  Length2 = 5
  Profile = -> Sketch005
  ReferenceAxis = -> Sketch005 [N_Axis]
  Reversed = true
  SideType = 0
  Suppressed = false
  Type = 0
  Type2 = 0
  expr: Length = VarSet001.woofer_rebate_depth
FEATURE [PartDesign::Chamfer] Chamfer001  label="woofer rebate chamfer"
  Angle = 45
  Base = -> Pocket [Edge35,Edge34]
  BaseFeature = -> Pocket
  ChamferType = 1
  FlipDirection = false
  Size = 6
  Size2 = 2
  SupportTransform = false
  Suppressed = false
  UseAllEdges = false
FEATURE [PartDesign::Pocket] Pocket001  label="woofer holes"
  BaseFeature = -> Chamfer001
  Direction = (0,0,-1)
  Length = 20
  Length2 = 5
  Profile = -> Sketch007
  ReferenceAxis = -> Sketch007 [N_Axis]
  Reversed = true
  SideType = 0
  Suppressed = false
  Type = 0
  Type2 = 0
FEATURE [PartDesign::Hole] Hole  label="woofer screw holes"
  BaseFeature = -> Pocket001
  BaseProfileType = 7
  CustomThreadClearance = 0
  Depth = 25
  DepthType = 0
  Diameter = 4.5
  DrillForDepth = false
  DrillPoint = 1
  DrillPointAngle = 118
  HoleCutCountersinkAngle = 90
  HoleCutCustomValues = false
  HoleCutDepth = 0
  HoleCutDiameter = 0
  HoleCutType = 0
  ModelThread = false
  Profile = -> Sketch011
  Reversed = true
  Suppressed = false
  Tapered = false
  TaperedAngle = 90
  ThreadClass = 0
  ThreadDepth = 25
  ThreadDepthType = 0
  ThreadDiameter = 4
  ThreadDirection = 0
  ThreadFit = 0
  ThreadSize = 11
  ThreadType = 1
  Threaded = false
  UseCustomThreadClearance = false
FEATURE [PartDesign::Pad] Pad003  label="bmr support ring"
  BaseFeature = -> Hole
  Direction = (0,0,1)
  Length = 5
  Length2 = 10
  Profile = -> Sketch009
  ReferenceAxis = -> Sketch009 [N_Axis]
  SideType = 0
  Suppressed = false
  Type = 0
  Type2 = 0
  expr: Length = VarSet001.bmr_support_thickness
FEATURE [PartDesign::Pocket] Pocket002  label="bmr rebate pocket"
  BaseFeature = -> Pad003
  Direction = (0,0,-1)
  Length = 5.65
  Length2 = 5
  Profile = -> Sketch008
  ReferenceAxis = -> Sketch008 [N_Axis]
  Reversed = true
  SideType = 0
  Suppressed = false
  Type = 0
  Type2 = 0
  expr: Length = VarSet001.bmr_rebate_depth
FEATURE [PartDesign::Chamfer] Chamfer  label="bmr rebate chamfer"
  Angle = 45
  Base = -> Pocket002 [Edge5]
  BaseFeature = -> Pocket002
  ChamferType = 1
  FlipDirection = false
  Size = 6
  Size2 = 2
  SupportTransform = false
  Suppressed = false
  UseAllEdges = false
FEATURE [PartDesign::Pocket] Pocket003  label="bmr hole"
  BaseFeature = -> Chamfer
  Direction = (0,0,-1)
  Length = 20
  Length2 = 5
  Profile = -> Sketch010
  ReferenceAxis = -> Sketch010 [N_Axis]
  Reversed = true
  SideType = 0
  Suppressed = false
  Type = 0
  Type2 = 0
FEATURE [PartDesign::Chamfer] Chamfer002  label="bmr backside chamfer"
  Angle = 45
  Base = -> Pocket003 [Edge76]
  BaseFeature = -> Pocket003
  ChamferType = 0
  FlipDirection = false
  Size = 4
  Size2 = 1
  SupportTransform = false
  Suppressed = false
  UseAllEdges = false
FEATURE [PartDesign::Hole] Hole001  label="bmr screw holes"
  BaseFeature = -> Chamfer002
  BaseProfileType = 7
  CustomThreadClearance = 0
  Depth = 25
  DepthType = 0
  Diameter = 2.5
  DrillForDepth = false
  DrillPoint = 1
  DrillPointAngle = 118
  HoleCutCountersinkAngle = 90
  HoleCutCustomValues = false
  HoleCutDepth = 0
  HoleCutDiameter = 0
  HoleCutType = 0
  ModelThread = false
  Profile = -> Sketch012
  Reversed = true
  Suppressed = false
  Tapered = false
  TaperedAngle = 90
  ThreadClass = 0
  ThreadDepth = 25
  ThreadDepthType = 0
  ThreadDiameter = 3
  ThreadDirection = 0
  ThreadFit = 0
  ThreadSize = 9
  ThreadType = 1
  Threaded = true
  UseCustomThreadClearance = false
FEATURE [PartDesign::Pad] Pad001  label="screw posts pad"
  BaseFeature = -> Hole001
  Direction = (0,0,1)
  Length = 37.1
  Length2 = 10
  Profile = -> Sketch004
  ReferenceAxis = -> Sketch004 [N_Axis]
  SideType = 0
  Suppressed = false
  Type = 0
  Type2 = 0
  expr: Length = <<v>>.int_depth
FEATURE [PartDesign::Hole] Hole002  label="post screw holes"
  BaseFeature = -> Pad001
  BaseProfileType = 7
  CustomThreadClearance = 0
  Depth = 25
  DepthType = 0
  Diameter = 3.3
  DrillForDepth = false
  DrillPoint = 1
  DrillPointAngle = 118
  HoleCutCountersinkAngle = 90
  HoleCutCustomValues = false
  HoleCutDepth = 0
  HoleCutDiameter = 0
  HoleCutType = 0
  ModelThread = false
  Profile = -> Sketch013
  Suppressed = false
  Tapered = false
  TaperedAngle = 90
  ThreadClass = 0
  ThreadDepth = 25
  ThreadDepthType = 0
  ThreadDiameter = 4
  ThreadDirection = 0
  ThreadFit = 0
  ThreadSize = 11
  ThreadType = 1
  Threaded = true
  UseCustomThreadClearance = false
FEATURE [PartDesign::Body] Body
  AllowCompound = false
  Group = -> [Sketch002,Sketch,Sketch003,Pad,Fillet,Thickness,Pocket004,Pad004,Pad002,Pocket,Chamfer001,Pocket001,Hole,Pad003,Pocket002,Chamfer,Pocket003,Chamfer002,Hole001,Sketch004,Pad001,Sketch005,Sketch006,Sketch007,Sketch008,Sketch009,Sketch010,Sketch011,Sketch012,Sketch013,Hole002,Sketch014,Sketch015]
  Origin = -> Origin
  Tip = -> Hole002
FEATURE [TechDraw::DrawSVGTemplate] Template003
  Height = 210
  Orientation = 1
  Template = /Applications/FreeCAD.app/Contents/Resources/share/Mod/TechDraw/Templates/ISO/A4_Landscape_TD.svg
  Width = 297
FEATURE [TechDraw::DrawViewImage] ActiveView
  Height = 102.4
  ImageFile = <userpath>/Library/Caches/FreeCAD/Cache/FreeCAD_Doc_eb121f07-895d-47cb-800c-a6bea0ebb6c4_0e058e_119829/Page003ActiveViewwNrP5w.png
  LockPosition = false
  Rotation = 0
  ScaleType = 2
  Width = 128
  X = 82.0287
  Y = 143.216
FEATURE [TechDraw::DrawViewImage] ActiveView001
  Height = 102.4
  ImageFile = <userpath>/Library/Caches/FreeCAD/Cache/FreeCAD_Doc_eb121f07-895d-47cb-800c-a6bea0ebb6c4_0e058e_119829/Page003ActiveView001LiKrpY.png
  LockPosition = false
  Rotation = 0
  ScaleType = 2
  Width = 128
  X = 207.459
  Y = 143.216
FEATURE [TechDraw::DrawPage] Page003  label="renders"
  KeepUpdated = true
  NextBalloonIndex = 1
  ProjectionType = 0
  Template = -> Template003
  Views = -> [ActiveView,ActiveView001]
FEATURE [Part::Feature] Body_cs  label="bmr_cs"
  shape: bbox 195 x 0.0005348 x 48 mm, 0 faces, 0 solids (baked)
FEATURE [Part::Feature] Body_cs001  label="woofer_cs"
  shape: bbox 195 x 0.0005348 x 48 mm, 0 faces, 0 solids (baked)
FEATURE [TechDraw::DrawProjGroupItem] View
  CoarseView = false
  Direction = (0,-1,0)
  Focus = 100
  HardHidden = false
  IsoCount = 0
  IsoHidden = false
  IsoVisible = false
  LockPosition = false
  Perspective = false
  Rotation = 0
  RotationVector = (1,0,0)
  ScaleType = 0
  ScrubCount = 1
  SeamHidden = false
  SeamVisible = false
  SmoothHidden = false
  SmoothVisible = true
  Source = -> [Body_cs]
  Type = 0
  X = 139.152
  XDirection = (1,0,0)
  Y = 92.5034
FEATURE [TechDraw::DrawProjGroupItem] View001
  CoarseView = false
  Direction = (0,-1,0)
  Focus = 100
  HardHidden = false
  IsoCount = 0
  IsoHidden = false
  IsoVisible = false
  LockPosition = false
  Perspective = false
  Rotation = 0
  RotationVector = (1,0,0)
  ScaleType = 0
  ScrubCount = 1
  SeamHidden = false
  SeamVisible = false
  SmoothHidden = false
  SmoothVisible = true
  Source = -> [Body_cs001]
  Type = 0
  X = 139.152
  XDirection = (1,0,0)
  Y = 158.502
FEATURE [TechDraw::DrawProjGroupItem] View002
  CoarseView = false
  Direction = (0,0,1)
  Focus = 100
  HardHidden = false
  IsoCount = 0
  IsoHidden = false
  IsoVisible = false
  LockPosition = false
  Perspective = false
  Rotation = 0
  RotationVector = (1,0,0)
  Scale = 0.5
  ScaleType = 2
  ScrubCount = 1
  SeamHidden = false
  SeamVisible = false
  SmoothHidden = false
  SmoothVisible = true
  Source = -> [Body]
  Type = 0
  X = 146.976
  XDirection = (3e-16,-1,0)
  Y = 133.819
FEATURE [TechDraw::DrawProjGroupItem] View003
  CoarseView = false
  Direction = (0,0,-1)
  Focus = 100
  HardHidden = false
  IsoCount = 0
  IsoHidden = false
  IsoVisible = false
  LockPosition = false
  Perspective = false
  Rotation = 0
  RotationVector = (1,0,0)
  Scale = 0.5
  ScaleType = 2
  ScrubCount = 1
  SeamHidden = false
  SeamVisible = false
  SmoothHidden = false
  SmoothVisible = true
  Source = -> [Body]
  Type = 0
  X = 147.219
  XDirection = (1e-16,1,0)
  Y = 134.934
FEATURE [TechDraw::DrawViewDimension] Dimension002
  AngleOverride = false
  Arbitrary = false
  ArbitraryTolerances = false
  BoxCorners = (2) [(-97.5,-24,0),(97.5,24,0)]
  EqualTolerance = true
  ExtensionAngle = 0
  FormatSpec = %.2w
  FormatSpecOverTolerance = %+.2w
  FormatSpecUnderTolerance = %+.2w
  Inverted = false
  LineAngle = 0
  LockPosition = false
  MeasureType = 1
  OverTolerance = 0
  References2D = -> [View001]
  Rotation = 0
  ScaleType = 0
  ShowUnits = false
  TheoreticalExact = false
  Type = 1
  UnderTolerance = 0
  UseActualArea = true
  X = -79.25
  Y = -29.5533
FEATURE [TechDraw::DrawViewDimension] Dimension003
  AngleOverride = false
  Arbitrary = false
  ArbitraryTolerances = false
  BoxCorners = (2) [(-97.5,-24,0),(97.5,24,0)]
  EqualTolerance = true
  ExtensionAngle = 0
  FormatSpec = %.2w
  FormatSpecOverTolerance = %+.2w
  FormatSpecUnderTolerance = %+.2w
  Inverted = false
  LineAngle = 0
  LockPosition = false
  MeasureType = 1
  OverTolerance = 0
  References2D = -> [View001]
  Rotation = 0
  ScaleType = 0
  ShowUnits = false
  TheoreticalExact = false
  Type = 2
  UnderTolerance = 0
  UseActualArea = true
  X = -66.4475
  Y = -29.3171
FEATURE [TechDraw::DrawViewDimension] Dimension005
  AngleOverride = false
  Arbitrary = false
  ArbitraryTolerances = false
  BoxCorners = (2) [(-97.5,-24,0),(97.5,24,0)]
  EqualTolerance = true
  ExtensionAngle = 0
  FormatSpec = %.2w
  FormatSpecOverTolerance = %+.2w
  FormatSpecUnderTolerance = %+.2w
  Inverted = false
  LineAngle = 0
  LockPosition = false
  MeasureType = 1
  OverTolerance = 0
  References2D = -> [View001]
  Rotation = 0
  ScaleType = 0
  ShowUnits = false
  TheoreticalExact = false
  Type = 2
  UnderTolerance = 0
  UseActualArea = true
  X = -69.1873
  Y = 13.0686
FEATURE [TechDraw::DrawViewDimension] Dimension010
  AngleOverride = false
  Arbitrary = false
  ArbitraryTolerances = false
  BoxCorners = (2) [(-97.5,-24,0),(97.5,24,0)]
  EqualTolerance = true
  ExtensionAngle = 0
  FormatSpec = %.2w
  FormatSpecOverTolerance = %+.2w
  FormatSpecUnderTolerance = %+.2w
  Inverted = false
  LineAngle = 0
  LockPosition = false
  MeasureType = 1
  OverTolerance = 0
  References2D = -> [View]
  Rotation = 0
  ScaleType = 0
  ShowUnits = false
  TheoreticalExact = false
  Type = 1
  UnderTolerance = 0
  UseActualArea = true
  X = -12.5
  Y = 1.32326
FEATURE [TechDraw::DrawViewDimension] Dimension013
  AngleOverride = false
  Arbitrary = false
  ArbitraryTolerances = false
  BoxCorners = (2) [(-97.5,-24,0),(97.5,24,0)]
  EqualTolerance = true
  ExtensionAngle = 0
  FormatSpec = %.2w
  FormatSpecOverTolerance = %+.2w
  FormatSpecUnderTolerance = %+.2w
  Inverted = false
  LineAngle = 0
  LockPosition = false
  MeasureType = 1
  OverTolerance = 0
  References2D = -> [View]
  Rotation = 0
  ScaleType = 0
  ShowUnits = false
  TheoreticalExact = false
  Type = 0
  UnderTolerance = 0
  UseActualArea = true
  X = 112.527
  Y = -14.9414
FEATURE [TechDraw::DrawViewDimension] Dimension014
  AngleOverride = false
  Arbitrary = false
  ArbitraryTolerances = false
  BoxCorners = (2) [(-97.5,-24,0),(97.5,24,0)]
  EqualTolerance = true
  ExtensionAngle = 0
  FormatSpec = %.2w
  FormatSpecOverTolerance = %+.2w
  FormatSpecUnderTolerance = %+.2w
  Inverted = false
  LineAngle = 0
  LockPosition = false
  MeasureType = 1
  OverTolerance = 0
  References2D = -> [View001]
  Rotation = 0
  ScaleType = 0
  ShowUnits = false
  TheoreticalExact = false
  Type = 2
  UnderTolerance = 0
  UseActualArea = true
  X = 31.0954
  Y = -9.48029
FEATURE [TechDraw::DrawViewDimension] Dimension
  AngleOverride = false
  Arbitrary = false
  ArbitraryTolerances = false
  BoxCorners = (2) [(-97.5,-24,0),(97.5,24,0)]
  EqualTolerance = true
  ExtensionAngle = 0
  FormatSpec = %.2w
  FormatSpecOverTolerance = %+.2w
  FormatSpecUnderTolerance = %+.2w
  Inverted = false
  LineAngle = 0
  LockPosition = false
  MeasureType = 1
  OverTolerance = 0
  References2D = -> [View]
  Rotation = 0
  ScaleType = 0
  ShowUnits = false
  TheoreticalExact = false
  Type = 2
  UnderTolerance = 0
  UseActualArea = true
  X = -88.3712
  Y = 5
FEATURE [TechDraw::DrawViewDimension] Dimension016
  AngleOverride = false
  Arbitrary = false
  ArbitraryTolerances = false
  BoxCorners = (2) [(-97.5,-24,0),(97.5,24,0)]
  EqualTolerance = true
  ExtensionAngle = 0
  FormatSpec = %.2w
  FormatSpecOverTolerance = %+.2w
  FormatSpecUnderTolerance = %+.2w
  Inverted = false
  LineAngle = 0
  LockPosition = false
  MeasureType = 1
  OverTolerance = 0
  References2D = -> [View001]
  Rotation = 0
  ScaleType = 0
  ShowUnits = false
  TheoreticalExact = false
  Type = 0
  UnderTolerance = 0
  UseActualArea = true
  X = 105.443
  Y = -6.825
FEATURE [TechDraw::DrawViewDimension] Dimension018
  AngleOverride = false
  Arbitrary = false
  ArbitraryTolerances = false
  BoxCorners = (2) [(-97.5,-24,0),(97.5,24,0)]
  EqualTolerance = true
  ExtensionAngle = 0
  FormatSpec = %.2w
  FormatSpecOverTolerance = %+.2w
  FormatSpecUnderTolerance = %+.2w
  Inverted = false
  LineAngle = 0
  LockPosition = false
  MeasureType = 1
  OverTolerance = 0
  References2D = -> [View001]
  Rotation = 0
  ScaleType = 0
  ShowUnits = false
  TheoreticalExact = false
  Type = 2
  UnderTolerance = 0
  UseActualArea = true
  X = 71.1934
  Y = 12.7508
FEATURE [TechDraw::DrawViewDimension] Dimension019
  AngleOverride = false
  Arbitrary = false
  ArbitraryTolerances = false
  BoxCorners = (2) [(-97.5,-24,0),(97.5,24,0)]
  EqualTolerance = true
  ExtensionAngle = 0
  FormatSpec = %.2w
  FormatSpecOverTolerance = %+.2w
  FormatSpecUnderTolerance = %+.2w
  Inverted = false
  LineAngle = 0
  LockPosition = false
  MeasureType = 1
  OverTolerance = 0
  References2D = -> [View001]
  Rotation = 0
  ScaleType = 0
  ShowUnits = false
  TheoreticalExact = false
  Type = 2
  UnderTolerance = 0
  UseActualArea = true
  X = 47.9859
  Y = -6.12158
FEATURE [TechDraw::DrawViewDimension] Dimension022
  AngleOverride = false
  Arbitrary = false
  ArbitraryTolerances = false
  BoxCorners = (2) [(-97.5,-24,0),(97.5,24,0)]
  EqualTolerance = true
  ExtensionAngle = 0
  FormatSpec = %.2w
  FormatSpecOverTolerance = %+.2w
  FormatSpecUnderTolerance = %+.2w
  Inverted = false
  LineAngle = 0
  LockPosition = false
  MeasureType = 1
  OverTolerance = 0
  References2D = -> [View]
  Rotation = 0
  ScaleType = 0
  ShowUnits = false
  TheoreticalExact = false
  Type = 1
  UnderTolerance = 0
  UseActualArea = true
  X = -4
  Y = -40.7804
FEATURE [TechDraw::DrawViewDimension] Dimension023
  AngleOverride = false
  Arbitrary = false
  ArbitraryTolerances = false
  BoxCorners = (2) [(-97.5,-24,0),(97.5,24,0)]
  EqualTolerance = true
  ExtensionAngle = 0
  FormatSpec = %.2w
  FormatSpecOverTolerance = %+.2w
  FormatSpecUnderTolerance = %+.2w
  Inverted = false
  LineAngle = 0
  LockPosition = false
  MeasureType = 1
  OverTolerance = 0
  References2D = -> [View]
  Rotation = 0
  ScaleType = 0
  ShowUnits = false
  TheoreticalExact = false
  Type = 2
  UnderTolerance = 0
  UseActualArea = true
  X = -36.0634
  Y = -29.1585
FEATURE [TechDraw::DrawViewDimension] Dimension024
  AngleOverride = false
  Arbitrary = false
  ArbitraryTolerances = false
  BoxCorners = (2) [(-97.5,-24,0),(97.5,24,0)]
  EqualTolerance = true
  ExtensionAngle = 0
  FormatSpec = %.2w
  FormatSpecOverTolerance = %+.2w
  FormatSpecUnderTolerance = %+.2w
  Inverted = false
  LineAngle = 0
  LockPosition = false
  MeasureType = 1
  OverTolerance = 0
  References2D = -> [View]
  Rotation = 0
  ScaleType = 0
  ShowUnits = false
  TheoreticalExact = false
  Type = 1
  UnderTolerance = 0
  UseActualArea = true
  X = 95
  Y = 35.0106
FEATURE [TechDraw::DrawViewDimension] Dimension026
  AngleOverride = false
  Arbitrary = false
  ArbitraryTolerances = false
  BoxCorners = (2) [(-123.75,-48.75,-1e-07),(123.75,48.75,1e-07)]
  EqualTolerance = true
  ExtensionAngle = 0
  FormatSpec = ⌀%.2w
  FormatSpecOverTolerance = %+.2w
  FormatSpecUnderTolerance = %+.2w
  Inverted = false
  LineAngle = 0
  LockPosition = false
  MeasureType = 1
  OverTolerance = 0
  References2D = -> [View003]
  Rotation = 0
  ScaleType = 0
  ShowUnits = false
  TheoreticalExact = false
  Type = 5
  UnderTolerance = 0
  UseActualArea = true
  X = -67.7964
  Y = 13.2495
FEATURE [TechDraw::DrawViewDimension] Dimension027
  AngleOverride = false
  Arbitrary = false
  ArbitraryTolerances = false
  BoxCorners = (2) [(-123.75,-48.75,-1e-07),(123.75,48.75,1e-07)]
  EqualTolerance = true
  ExtensionAngle = 0
  FormatSpec = ⌀%.2w
  FormatSpecOverTolerance = %+.2w
  FormatSpecUnderTolerance = %+.2w
  Inverted = false
  LineAngle = 0
  LockPosition = false
  MeasureType = 1
  OverTolerance = 0
  References2D = -> [View003]
  Rotation = 0
  ScaleType = 0
  ShowUnits = false
  TheoreticalExact = false
  Type = 5
  UnderTolerance = 0
  UseActualArea = true
  X = -46.8036
  Y = 8.77568
FEATURE [TechDraw::DrawViewDimension] Dimension028
  AngleOverride = false
  Arbitrary = false
  ArbitraryTolerances = false
  BoxCorners = (2) [(-123.75,-48.75,-1e-07),(123.75,48.75,1e-07)]
  EqualTolerance = true
  ExtensionAngle = 0
  FormatSpec = ⌀%.2w
  FormatSpecOverTolerance = %+.2w
  FormatSpecUnderTolerance = %+.2w
  Inverted = false
  LineAngle = 0
  LockPosition = false
  MeasureType = 1
  OverTolerance = 0
  References2D = -> [View003]
  Rotation = 0
  ScaleType = 0
  ShowUnits = false
  TheoreticalExact = false
  Type = 5
  UnderTolerance = 0
  UseActualArea = true
  X = -9.02964
  Y = 8.42399
FEATURE [TechDraw::DrawViewDimension] Dimension029
  AngleOverride = false
  Arbitrary = false
  ArbitraryTolerances = false
  BoxCorners = (2) [(-123.75,-48.75,-1e-07),(123.75,48.75,1e-07)]
  EqualTolerance = true
  ExtensionAngle = 0
  FormatSpec = ⌀%.2w
  FormatSpecOverTolerance = %+.2w
  FormatSpecUnderTolerance = %+.2w
  Inverted = false
  LineAngle = 0
  LockPosition = false
  MeasureType = 1
  OverTolerance = 0
  References2D = -> [View003]
  Rotation = 0
  ScaleType = 0
  ShowUnits = false
  TheoreticalExact = false
  Type = 5
  UnderTolerance = 0
  UseActualArea = true
  X = 8.25946
  Y = 8.43153
FEATURE [TechDraw::DrawViewDimension] Dimension030
  AngleOverride = false
  Arbitrary = false
  ArbitraryTolerances = false
  BoxCorners = (2) [(-123.75,-48.75,-1e-07),(123.75,48.75,1e-07)]
  EqualTolerance = true
  ExtensionAngle = 0
  FormatSpec = %.2w
  FormatSpecOverTolerance = %+.2w
  FormatSpecUnderTolerance = %+.2w
  Inverted = false
  LineAngle = 0
  LockPosition = false
  MeasureType = 1
  OverTolerance = 0
  References2D = -> [View003]
  Rotation = 0
  ScaleType = 0
  ShowUnits = false
  TheoreticalExact = false
  Type = 1
  UnderTolerance = 0
  UseActualArea = true
  X = 61.2867
  Y = -57.9698
FEATURE [TechDraw::DrawViewDimension] Dimension031
  AngleOverride = false
  Arbitrary = false
  ArbitraryTolerances = false
  BoxCorners = (2) [(-123.75,-48.75,-1e-07),(123.75,48.75,1e-07)]
  EqualTolerance = true
  ExtensionAngle = 0
  FormatSpec = %.2w
  FormatSpecOverTolerance = %+.2w
  FormatSpecUnderTolerance = %+.2w
  Inverted = false
  LineAngle = 0
  LockPosition = false
  MeasureType = 1
  OverTolerance = 0
  References2D = -> [View003]
  Rotation = 0
  ScaleType = 0
  ShowUnits = false
  TheoreticalExact = false
  Type = 2
  UnderTolerance = 0
  UseActualArea = true
  X = -24.5474
  Y = -23.3833
FEATURE [TechDraw::DrawViewDimension] Dimension032
  AngleOverride = false
  Arbitrary = false
  ArbitraryTolerances = false
  BoxCorners = (2) [(-123.75,-48.75,-1e-07),(123.75,48.75,1e-07)]
  EqualTolerance = true
  ExtensionAngle = 0
  FormatSpec = %.2w
  FormatSpecOverTolerance = %+.2w
  FormatSpecUnderTolerance = %+.2w
  Inverted = false
  LineAngle = 0
  LockPosition = false
  MeasureType = 1
  OverTolerance = 0
  References2D = -> [View003]
  Rotation = 0
  ScaleType = 0
  ShowUnits = false
  TheoreticalExact = false
  Type = 0
  UnderTolerance = 0
  UseActualArea = true
  X = 119.722
  Y = 62.9969
FEATURE [TechDraw::DrawViewDimension] Dimension033
  AngleOverride = false
  Arbitrary = false
  ArbitraryTolerances = false
  BoxCorners = (2) [(-123.75,-48.75,-1e-07),(123.75,48.75,1e-07)]
  EqualTolerance = true
  ExtensionAngle = 0
  FormatSpec = %.2w
  FormatSpecOverTolerance = %+.2w
  FormatSpecUnderTolerance = %+.2w
  Inverted = false
  LineAngle = 0
  LockPosition = false
  MeasureType = 1
  OverTolerance = 0
  References2D = -> [View003]
  Rotation = 0
  ScaleType = 0
  ShowUnits = false
  TheoreticalExact = false
  Type = 0
  UnderTolerance = 0
  UseActualArea = true
  X = 127.063
  Y = -61.2391
FEATURE [TechDraw::DrawViewDimension] Dimension034
  AngleOverride = false
  Arbitrary = false
  ArbitraryTolerances = false
  BoxCorners = (2) [(-123.75,-48.75,-1e-07),(123.75,48.75,1e-07)]
  EqualTolerance = true
  ExtensionAngle = 0
  FormatSpec = %.2w
  FormatSpecOverTolerance = %+.2w
  FormatSpecUnderTolerance = %+.2w
  Inverted = false
  LineAngle = 0
  LockPosition = false
  MeasureType = 1
  OverTolerance = 0
  References2D = -> [View003]
  Rotation = 0
  ScaleType = 0
  ShowUnits = false
  TheoreticalExact = false
  Type = 0
  UnderTolerance = 0
  UseActualArea = true
  X = 69.1681
  Y = 13.1938
FEATURE [TechDraw::DrawViewDimension] Dimension035
  AngleOverride = false
  Arbitrary = false
  ArbitraryTolerances = false
  BoxCorners = (2) [(-123.75,-48.75,-1e-07),(123.75,48.75,1e-07)]
  EqualTolerance = true
  ExtensionAngle = 0
  FormatSpec = %.2w
  FormatSpecOverTolerance = %+.2w
  FormatSpecUnderTolerance = %+.2w
  Inverted = false
  LineAngle = 0
  LockPosition = false
  MeasureType = 1
  OverTolerance = 0
  References2D = -> [View003]
  Rotation = 0
  ScaleType = 0
  ShowUnits = false
  TheoreticalExact = false
  Type = 0
  UnderTolerance = 0
  UseActualArea = true
  X = -12.2423
  Y = -38.2173
FEATURE [TechDraw::DrawViewDimension] Dimension036
  AngleOverride = false
  Arbitrary = false
  ArbitraryTolerances = false
  BoxCorners = (2) [(-97.5,-24,0),(97.5,24,0)]
  EqualTolerance = true
  ExtensionAngle = 0
  FormatSpec = %.2w
  FormatSpecOverTolerance = %+.2w
  FormatSpecUnderTolerance = %+.2w
  Inverted = false
  LineAngle = 0
  LockPosition = false
  MeasureType = 1
  OverTolerance = 0
  References2D = -> [View]
  Rotation = 0
  ScaleType = 0
  ShowUnits = false
  TheoreticalExact = false
  Type = 2
  UnderTolerance = 0
  UseActualArea = true
  X = -24.5896
  Y = -19.3182
FEATURE [TechDraw::DrawViewDimension] Dimension017
  AngleOverride = false
  Arbitrary = false
  ArbitraryTolerances = false
  BoxCorners = (2) [(-97.5,-24,0),(97.5,24,0)]
  EqualTolerance = true
  ExtensionAngle = 0
  FormatSpec = %.2w
  FormatSpecOverTolerance = %+.2w
  FormatSpecUnderTolerance = %+.2w
  Inverted = false
  LineAngle = 0
  LockPosition = false
  MeasureType = 1
  OverTolerance = 0
  References2D = -> [View001]
  Rotation = 0
  ScaleType = 0
  ShowUnits = false
  TheoreticalExact = false
  Type = 2
  UnderTolerance = 0
  UseActualArea = true
  X = 117.054
  Y = 0
FEATURE [TechDraw::DrawViewDimension] Dimension039
  AngleOverride = false
  Arbitrary = false
  ArbitraryTolerances = false
  BoxCorners = (2) [(-97.5,-24,0),(97.5,24,0)]
  EqualTolerance = true
  ExtensionAngle = 0
  FormatSpec = %.2w
  FormatSpecOverTolerance = %+.2w
  FormatSpecUnderTolerance = %+.2w
  Inverted = false
  LineAngle = 0
  LockPosition = false
  MeasureType = 1
  OverTolerance = 0
  References2D = -> [View001]
  Rotation = 0
  ScaleType = 0
  ShowUnits = false
  TheoreticalExact = false
  Type = 1
  UnderTolerance = 0
  UseActualArea = true
  X = -92.4743
  Y = 32.9307
FEATURE [TechDraw::DrawViewDimension] Dimension040
  AngleOverride = false
  Arbitrary = false
  ArbitraryTolerances = false
  BoxCorners = (2) [(-97.5,-24,0),(97.5,24,0)]
  EqualTolerance = true
  ExtensionAngle = 0
  FormatSpec = %.2w
  FormatSpecOverTolerance = %+.2w
  FormatSpecUnderTolerance = %+.2w
  Inverted = false
  LineAngle = 0
  LockPosition = false
  MeasureType = 1
  OverTolerance = 0
  References2D = -> [View001]
  Rotation = 0
  ScaleType = 0
  ShowUnits = false
  TheoreticalExact = false
  Type = 0
  UnderTolerance = 0
  UseActualArea = true
  X = -83.0706
  Y = 8.26113
FEATURE [App::Point] Origin003
  Role = Origin
FEATURE [Sketcher::SketchObject] Sketch016
  ArcFitTolerance = 1e-06
  AttachmentOffset = pos=(0,0,48) rot=(0,0,1;0rad)
  AttachmentSupport = -> [Origin002]
  ExternalTypes = [0]
  FullyConstrained = true
  MakeInternals = false
  MapMode = 5
  Placement = pos=(0,0,48) rot=(0,0,1;0rad)
  expr: .AttachmentOffset.Base.z = <<v>>.ext_depth
  expr: Constraints[17] = <<v>>.backplate_width
  expr: Constraints[18] = <<v>>.backplate_height
  expr: Constraints[19] = <<v>>.ext_roundover - <<v>>.rim_width
  sketch-geometry (10):
    g0: LineSegment StartX=-94.9 StartY=237.4 StartZ=0 EndX=-94.9 EndY=-237.4 EndZ=0
    g1: LineSegment StartX=-87.4 StartY=-244.9 StartZ=0 EndX=87.4 EndY=-244.9 EndZ=0
    g2: LineSegment StartX=94.9 StartY=-237.4 StartZ=0 EndX=94.9 EndY=237.4 EndZ=0
    g3: LineSegment StartX=87.4 StartY=244.9 StartZ=0 EndX=-87.4 EndY=244.9 EndZ=0
    g4: ArcOfCircle CenterX=-87.4 CenterY=237.4 CenterZ=0 NormalX=0 NormalY=0 NormalZ=1 AngleXU=0 Radius=7.5 StartAngle=1.5708 EndAngle=3.14159
    g5: ArcOfCircle CenterX=-87.4 CenterY=-237.4 CenterZ=0 NormalX=0 NormalY=0 NormalZ=1 AngleXU=0 Radius=7.5 StartAngle=3.14159 EndAngle=4.71239
    g6: ArcOfCircle CenterX=87.4 CenterY=-237.4 CenterZ=0 NormalX=0 NormalY=0 NormalZ=1 AngleXU=0 Radius=7.5 StartAngle=4.71239 EndAngle=6.28319
    g7: ArcOfCircle CenterX=87.4 CenterY=237.4 CenterZ=0 NormalX=0 NormalY=0 NormalZ=1 AngleXU=0 Radius=7.5 StartAngle=9e-16 EndAngle=1.5708
    g8: GeomPoint [constr] X=-94.9 Y=244.9 Z=0
    g9: GeomPoint [constr] X=94.9 Y=-244.9 Z=0
  constraints (22):
    c: Tangent(g0,g4) = -1.5708
    c: Tangent(g0,g5) = -1.5708
    c: Tangent(g1,g5) = -1.5708
    c: Tangent(g1,g6) = -1.5708
    c: Tangent(g2,g6) = -1.5708
    c: Tangent(g2,g7) = -1.5708
    c: Tangent(g3,g7) = -1.5708
    c: Tangent(g3,g4) = -1.5708
    c: Vertical(g0)
    c: Vertical(g2)
    c: Horizontal(g1)
    c: Equal(g5,g6)
    c: Equal(g6,g7)
    c: PointOnObject(g8,g0)
    c: PointOnObject(g8,g3)
    c: PointOnObject(g9,g1)
    c: PointOnObject(g9,g2)
    c: Distance(g2,g0) = 189.8
    c: Distance(g1,g3) = 489.8
    c: Radius(g6) = 7.5
    c: Symmetric(g3,g3,g-2)
    c: Symmetric(g3,g1,g-1)
FEATURE [PartDesign::Pad] Pad005
  Direction = (0,0,1)
  Length = 5
  Length2 = 10
  Profile = -> Sketch016
  ReferenceAxis = -> Sketch016 [N_Axis]
  Reversed = true
  SideType = 0
  Suppressed = false
  Type = 0
  Type2 = 0
  expr: Length = <<v>>.backplate_thickness
FEATURE [Sketcher::SketchObject] Sketch017
  ArcFitTolerance = 1e-06
  AttachmentSupport = -> [Pad005]
  ExternalTypes = [0]
  FullyConstrained = true
  MakeInternals = false
  MapMode = 5
  Placement = pos=(0,0,48) rot=(0,0,1;0rad)
  expr: Constraints[11] = Sketch013.Constraints[11]
  expr: Constraints[1] = Sketch013.Constraints[1]
  expr: Constraints[2] = Sketch013.Constraints[2]
  expr: Constraints[8] = Sketch013.Constraints[8]
  expr: Constraints[9] = Sketch013.Constraints[9]
  sketch-geometry (9):
    g0: GeomPoint X=-87.5 Y=237.5 Z=0
    g1: GeomPoint X=87.5 Y=237.5 Z=0
    g2: GeomPoint X=87.5 Y=-237.5 Z=0
    g3: GeomPoint X=-87.5 Y=-237.5 Z=0
    g4: GeomPoint X=-87.5 Y=-67.5 Z=0
    g5: GeomPoint X=-87.5 Y=67.5 Z=0
    g6: GeomPoint X=87.5 Y=67.5 Z=0
    g7: GeomPoint X=87.5 Y=-67.5 Z=0
    g8: GeomPoint X=20 Y=0 Z=0
  constraints (12):
    c: PointOnObject(g8,g-1)
    c: DistanceY(g-1,g0) = 237.5
    c: DistanceX(g0,g-1) = 87.5
    c: Symmetric(g0,g1,g-2)
    c: Symmetric(g5,g6,g-2)
    c: Symmetric(g4,g7,g-2)
    c: Symmetric(g3,g2,g-2)
    c: Symmetric(g2,g1,g-1)
    c: DistanceX(g5,g-1) = 87.5
    c: DistanceY(g4,g5) = 135
    c: Symmetric(g5,g4,g-1)
    c: DistanceX(g-1,g8) = 20
FEATURE [PartDesign::Hole] Hole003
  BaseFeature = -> Pad005
  BaseProfileType = 7
  CustomThreadClearance = 0
  Depth = 5
  DepthType = 0
  Diameter = 4.5
  DrillForDepth = false
  DrillPoint = 1
  DrillPointAngle = 118
  HoleCutCountersinkAngle = 90
  HoleCutCustomValues = false
  HoleCutDepth = 4.5
  HoleCutDiameter = 9
  HoleCutType = 2
  ModelThread = false
  Profile = -> Sketch017
  Suppressed = false
  Tapered = false
  TaperedAngle = 90
  ThreadClass = 0
  ThreadDepth = 5
  ThreadDepthType = 0
  ThreadDiameter = 4
  ThreadDirection = 0
  ThreadFit = 0
  ThreadSize = 11
  ThreadType = 1
  Threaded = false
  UseCustomThreadClearance = false
  expr: Depth = <<v>>.backplate_thickness
FEATURE [PartDesign::Body] Body001  label="backplate"
  AllowCompound = false
  Group = -> [Sketch016,Pad005,Sketch017,Hole003]
  Origin = -> Origin002
  Tip = -> Hole003
FEATURE [TechDraw::DrawViewAnnotation] Annotation
  Font = osifont
  LineSpace = 100
  LockPosition = false
  MaxWidth = -1
  Rotation = 0
  ScaleType = 0
  Text = M4 threaded
  TextSize = 3
  TextStyle = 0
  X = 72.2188
  Y = 114.907
FEATURE [TechDraw::DrawViewAnnotation] Annotation001
  Font = osifont
  LineSpace = 100
  LockPosition = false
  MaxWidth = -1
  Rotation = 0
  ScaleType = 0
  Text = M4 threaded
  TextSize = 3
  TextStyle = 0
  X = 72.0467
  Y = 114.391
FEATURE [TechDraw::DrawViewAnnotation] Annotation002
  Font = osifont
  LineSpace = 100
  LockPosition = false
  MaxWidth = -1
  Rotation = 0
  ScaleType = 0
  Text = M4 threaded
  TextSize = 3
  TextStyle = 0
  X = 72.0467
  Y = 114.391
FEATURE [TechDraw::DrawViewAnnotation] Annotation003
  Font = osifont
  LineSpace = 100
  LockPosition = false
  MaxWidth = -1
  Rotation = 0
  ScaleType = 0
  Text = M4 threaded
  TextSize = 3
  TextStyle = 0
  X = 72.0467
  Y = 114.391
FEATURE [TechDraw::DrawViewAnnotation] Annotation004
  Font = osifont
  LineSpace = 100
  LockPosition = false
  MaxWidth = -1
  Rotation = 0
  ScaleType = 0
  Text = M4 threaded
  TextSize = 3
  TextStyle = 0
  X = 72.2188
  Y = 114.907
FEATURE [TechDraw::DrawViewAnnotation] Annotation005
  Font = osifont
  LineSpace = 100
  LockPosition = false
  MaxWidth = -1
  Rotation = 0
  ScaleType = 0
  Text = M3 threaded
  TextSize = 2.5
  TextStyle = 0
  X = 160.64
  Y = 112.571
FEATURE [TechDraw::DrawViewDimension] Dimension041
  AngleOverride = false
  Arbitrary = false
  ArbitraryTolerances = false
  BoxCorners = (2) [(-123.75,-48.75,0),(123.75,48.75,0)]
  EqualTolerance = true
  ExtensionAngle = 0
  FormatSpec = ⌀%.2w
  FormatSpecOverTolerance = %+.2w
  FormatSpecUnderTolerance = %+.2w
  Inverted = false
  LineAngle = 0
  LockPosition = false
  MeasureType = 1
  OverTolerance = 0
  References2D = -> [View002]
  Rotation = 0
  ScaleType = 0
  ShowUnits = false
  TheoreticalExact = false
  Type = 5
  UnderTolerance = 0
  UseActualArea = true
  X = -84.7852
  Y = -0.99516
FEATURE [TechDraw::DrawViewDimension] Dimension042
  AngleOverride = false
  Arbitrary = false
  ArbitraryTolerances = false
  BoxCorners = (2) [(-123.75,-48.75,0),(123.75,48.75,0)]
  EqualTolerance = true
  ExtensionAngle = 0
  FormatSpec = ⌀%.2w
  FormatSpecOverTolerance = %+.2w
  FormatSpecUnderTolerance = %+.2w
  Inverted = false
  LineAngle = 0
  LockPosition = false
  MeasureType = 1
  OverTolerance = 0
  References2D = -> [View002]
  Rotation = 0
  ScaleType = 0
  ShowUnits = false
  TheoreticalExact = false
  Type = 5
  UnderTolerance = 0
  UseActualArea = true
  X = -77.1872
  Y = 10.7151
FEATURE [TechDraw::DrawViewDimension] Dimension043
  AngleOverride = false
  Arbitrary = false
  ArbitraryTolerances = false
  BoxCorners = (2) [(-123.75,-48.75,0),(123.75,48.75,0)]
  EqualTolerance = true
  ExtensionAngle = 0
  FormatSpec = %.2w
  FormatSpecOverTolerance = %+.2w
  FormatSpecUnderTolerance = %+.2w
  Inverted = false
  LineAngle = 0
  LockPosition = false
  MeasureType = 1
  OverTolerance = 0
  References2D = -> [View002]
  Rotation = 0
  ScaleType = 0
  ShowUnits = false
  TheoreticalExact = false
  Type = 0
  UnderTolerance = 0
  UseActualArea = true
  X = -6.90557
  Y = -26.6256
FEATURE [TechDraw::DrawViewDimension] Dimension044
  AngleOverride = false
  Arbitrary = false
  ArbitraryTolerances = false
  BoxCorners = (2) [(-123.75,-48.75,0),(123.75,48.75,0)]
  EqualTolerance = true
  ExtensionAngle = 0
  FormatSpec = ⌀%.2w
  FormatSpecOverTolerance = %+.2w
  FormatSpecUnderTolerance = %+.2w
  Inverted = false
  LineAngle = 0
  LockPosition = false
  MeasureType = 1
  OverTolerance = 0
  References2D = -> [View002]
  Rotation = 0
  ScaleType = 0
  ShowUnits = false
  TheoreticalExact = false
  Type = 5
  UnderTolerance = 0
  UseActualArea = true
  X = -6.02985
  Y = -15.4398
FEATURE [TechDraw::DrawViewDimension] Dimension045
  AngleOverride = false
  Arbitrary = false
  ArbitraryTolerances = false
  BoxCorners = (2) [(-123.75,-48.75,0),(123.75,48.75,0)]
  EqualTolerance = true
  ExtensionAngle = 0
  FormatSpec = ⌀%.2w
  FormatSpecOverTolerance = %+.2w
  FormatSpecUnderTolerance = %+.2w
  Inverted = false
  LineAngle = 0
  LockPosition = false
  MeasureType = 1
  OverTolerance = 0
  References2D = -> [View002]
  Rotation = 0
  ScaleType = 0
  ShowUnits = false
  TheoreticalExact = false
  Type = 5
  UnderTolerance = 0
  UseActualArea = true
  X = 4.25424
  Y = -21.6438
FEATURE [TechDraw::DrawViewDimension] Dimension046
  AngleOverride = false
  Arbitrary = false
  ArbitraryTolerances = false
  BoxCorners = (2) [(-123.75,-48.75,0),(123.75,48.75,0)]
  EqualTolerance = true
  ExtensionAngle = 0
  FormatSpec = ⌀%.2w
  FormatSpecOverTolerance = %+.2w
  FormatSpecUnderTolerance = %+.2w
  Inverted = false
  LineAngle = 0
  LockPosition = false
  MeasureType = 1
  OverTolerance = 0
  References2D = -> [View002]
  Rotation = 0
  ScaleType = 0
  ShowUnits = false
  TheoreticalExact = false
  Type = 5
  UnderTolerance = 0
  UseActualArea = true
  X = -57.5067
  Y = -55.5981
FEATURE [TechDraw::DrawViewAnnotation] Annotation006
  Font = osifont
  LineSpace = 100
  LockPosition = false
  MaxWidth = -1
  Owner = -> View002
  Rotation = 0
  ScaleType = 0
  Text = M4 threaded
  TextSize = 4
  TextStyle = 0
  X = -102.151
  Y = -39.0017
FEATURE [TechDraw::DrawProjGroupItem] View004
  CoarseView = false
  Direction = (0,-1,0)
  Focus = 100
  HardHidden = false
  IsoCount = 0
  IsoHidden = false
  IsoVisible = false
  LockPosition = false
  Perspective = false
  Rotation = 0
  RotationVector = (1,0,0)
  Scale = 0.5
  ScaleType = 2
  ScrubCount = 1
  SeamHidden = false
  SeamVisible = false
  SmoothHidden = false
  SmoothVisible = true
  Source = -> [Body]
  Type = 0
  X = 79.4991
  XDirection = (-1,0,1e-16)
  Y = 50.4532
FEATURE [TechDraw::DrawViewDimension] Dimension047
  AngleOverride = false
  Arbitrary = false
  ArbitraryTolerances = false
  BoxCorners = (2) [(-48.75,-12,-1e-07),(48.75,12,1e-07)]
  EqualTolerance = true
  ExtensionAngle = 0
  FormatSpec = R%.2w
  FormatSpecOverTolerance = %+.2w
  FormatSpecUnderTolerance = %+.2w
  Inverted = false
  LineAngle = 0
  LockPosition = false
  MeasureType = 1
  OverTolerance = 0
  References2D = -> [View004]
  Rotation = 0
  ScaleType = 0
  ShowUnits = false
  TheoreticalExact = false
  Type = 4
  UnderTolerance = 0
  UseActualArea = true
  X = -52.9982
  Y = 22.0252
FEATURE [TechDraw::DrawPage] Page002  label="enclosure front view"
  KeepUpdated = true
  NextBalloonIndex = 1
  ProjectionType = 0
  Template = -> Template002
  Views = -> [View003,Dimension026,Dimension027,Dimension028,Dimension029,Dimension030,Dimension031,Dimension032,Dimension033,Dimension034,Dimension035,Annotation,Annotation005,View004,Dimension047]
FEATURE [TechDraw::DrawViewDimension] Dimension020
  AngleOverride = false
  Arbitrary = false
  ArbitraryTolerances = false
  BoxCorners = (2) [(-97.5,-24,0),(97.5,24,0)]
  EqualTolerance = true
  ExtensionAngle = 0
  FormatSpec = %.2w
  FormatSpecOverTolerance = %+.2w
  FormatSpecUnderTolerance = %+.2w
  Inverted = false
  LineAngle = 0
  LockPosition = false
  MeasureType = 1
  OverTolerance = 0
  References2D = -> [View]
  Rotation = 0
  ScaleType = 0
  ShowUnits = false
  TheoreticalExact = false
  Type = 0
  UnderTolerance = 0
  UseActualArea = true
  X = -55.9422
  Y = -35.2571
FEATURE [TechDraw::DrawViewDimension] Dimension048
  AngleOverride = false
  Arbitrary = false
  ArbitraryTolerances = false
  BoxCorners = (2) [(-97.5,-24,0),(97.5,24,0)]
  EqualTolerance = true
  ExtensionAngle = 0
  FormatSpec = %.2w
  FormatSpecOverTolerance = %+.2w
  FormatSpecUnderTolerance = %+.2w
  Inverted = false
  LineAngle = 0
  LockPosition = false
  MeasureType = 1
  OverTolerance = 0
  References2D = -> [View]
  Rotation = 0
  ScaleType = 0
  ShowUnits = false
  TheoreticalExact = false
  Type = 2
  UnderTolerance = 0
  UseActualArea = true
  X = -47.4615
  Y = -5.7216
FEATURE [TechDraw::DrawViewDimension] Dimension049
  AngleOverride = false
  Arbitrary = false
  ArbitraryTolerances = false
  BoxCorners = (2) [(-97.5,-24,0),(97.5,24,0)]
  EqualTolerance = true
  ExtensionAngle = 0
  FormatSpec = %.2w
  FormatSpecOverTolerance = %+.2w
  FormatSpecUnderTolerance = %+.2w
  Inverted = false
  LineAngle = 0
  LockPosition = false
  MeasureType = 1
  OverTolerance = 0
  References2D = -> [View]
  Rotation = 0
  ScaleType = 0
  ShowUnits = false
  TheoreticalExact = false
  Type = 2
  UnderTolerance = 0
  UseActualArea = true
  X = -112.276
  Y = -22.3181
FEATURE [TechDraw::DrawPage] Page001  label="driver cross sections"
  KeepUpdated = true
  NextBalloonIndex = 1
  ProjectionType = 0
  Template = -> Template001
  Views = -> [View,View001,Dimension002,Dimension003,Dimension005,Dimension010,Dimension013,Dimension014,Dimension,Dimension016,Dimension017,Dimension018,Dimension019,Dimension020,Dimension022,Dimension023,Dimension024,Dimension036,Dimension039,Dimension040,Dimension048,Dimension049]
FEATURE [TechDraw::DrawViewDimension] Dimension050
  AngleOverride = false
  Arbitrary = false
  ArbitraryTolerances = false
  BoxCorners = (2) [(-123.75,-48.75,0),(123.75,48.75,0)]
  EqualTolerance = true
  ExtensionAngle = 0
  FormatSpec = %.2w
  FormatSpecOverTolerance = %+.2w
  FormatSpecUnderTolerance = %+.2w
  Inverted = false
  LineAngle = 0
  LockPosition = false
  MeasureType = 1
  OverTolerance = 0
  References2D = -> [View002]
  Rotation = 0
  ScaleType = 0
  ShowUnits = false
  TheoreticalExact = false
  Type = 1
  UnderTolerance = 0
  UseActualArea = true
  X = 25.0727
  Y = -57.0904
FEATURE [TechDraw::DrawViewDimension] Dimension051
  AngleOverride = false
  Arbitrary = false
  ArbitraryTolerances = false
  BoxCorners = (2) [(-123.75,-48.75,0),(123.75,48.75,0)]
  EqualTolerance = true
  ExtensionAngle = 0
  FormatSpec = %.2w
  FormatSpecOverTolerance = %+.2w
  FormatSpecUnderTolerance = %+.2w
  Inverted = false
  LineAngle = 0
  LockPosition = false
  MeasureType = 1
  OverTolerance = 0
  References2D = -> [View002]
  Rotation = 0
  ScaleType = 0
  ShowUnits = false
  TheoreticalExact = false
  Type = 0
  UnderTolerance = 0
  UseActualArea = true
  X = -4.80314
  Y = 29.375
FEATURE [TechDraw::DrawViewDimension] Dimension052
  AngleOverride = false
  Arbitrary = false
  ArbitraryTolerances = false
  BoxCorners = (2) [(-123.75,-48.75,0),(123.75,48.75,0)]
  EqualTolerance = true
  ExtensionAngle = 0
  FormatSpec = %.2w
  FormatSpecOverTolerance = %+.2w
  FormatSpecUnderTolerance = %+.2w
  Inverted = false
  LineAngle = 0
  LockPosition = false
  MeasureType = 1
  OverTolerance = 0
  References2D = -> [View002]
  Rotation = 0
  ScaleType = 0
  ShowUnits = false
  TheoreticalExact = false
  Type = 0
  UnderTolerance = 0
  UseActualArea = true
  X = -22.1095
  Y = -32.0647
FEATURE [TechDraw::DrawViewDimension] Dimension053
  AngleOverride = false
  Arbitrary = false
  ArbitraryTolerances = false
  BoxCorners = (2) [(-123.75,-48.75,0),(123.75,48.75,0)]
  EqualTolerance = true
  ExtensionAngle = 0
  FormatSpec = %.2w
  FormatSpecOverTolerance = %+.2w
  FormatSpecUnderTolerance = %+.2w
  Inverted = false
  LineAngle = 0
  LockPosition = false
  MeasureType = 1
  OverTolerance = 0
  References2D = -> [View002]
  Rotation = 0
  ScaleType = 0
  ShowUnits = false
  TheoreticalExact = false
  Type = 0
  UnderTolerance = 0
  UseActualArea = true
  X = 44.7383
  Y = -1.04452
FEATURE [TechDraw::DrawViewDimension] Dimension054
  AngleOverride = false
  Arbitrary = false
  ArbitraryTolerances = false
  BoxCorners = (2) [(-123.75,-48.75,0),(123.75,48.75,0)]
  EqualTolerance = true
  ExtensionAngle = 0
  FormatSpec = %.2w
  FormatSpecOverTolerance = %+.2w
  FormatSpecUnderTolerance = %+.2w
  Inverted = false
  LineAngle = 0
  LockPosition = false
  MeasureType = 1
  OverTolerance = 0
  References2D = -> [View002]
  Rotation = 0
  ScaleType = 0
  ShowUnits = false
  TheoreticalExact = false
  Type = 1
  UnderTolerance = 0
  UseActualArea = true
  X = -12.124
  Y = 19.4224
FEATURE [TechDraw::DrawViewDimension] Dimension055
  AngleOverride = false
  Arbitrary = false
  ArbitraryTolerances = false
  BoxCorners = (2) [(-123.75,-48.75,0),(123.75,48.75,0)]
  EqualTolerance = true
  ExtensionAngle = 0
  FormatSpec = R%.2w
  FormatSpecOverTolerance = %+.2w
  FormatSpecUnderTolerance = %+.2w
  Inverted = false
  LineAngle = 0
  LockPosition = false
  MeasureType = 1
  OverTolerance = 0
  References2D = -> [View002]
  Rotation = 0
  ScaleType = 0
  ShowUnits = false
  TheoreticalExact = false
  Type = 4
  UnderTolerance = 0
  UseActualArea = true
  X = 19.9872
  Y = 24.3044
FEATURE [TechDraw::DrawPage] Page  label="enclosure back view"
  KeepUpdated = true
  NextBalloonIndex = 1
  ProjectionType = 0
  Template = -> Template
  Views = -> [View002,Dimension041,Dimension042,Dimension043,Dimension044,Dimension045,Dimension046,Annotation006,Dimension050,Dimension051,Dimension052,Dimension053,Dimension054,Dimension055]
FEATURE [App::DocumentObjectGroup] Group  label="Drawings"
  Group = -> [Page002,Page,Page001,Page003,Body_cs,Body_cs001]
